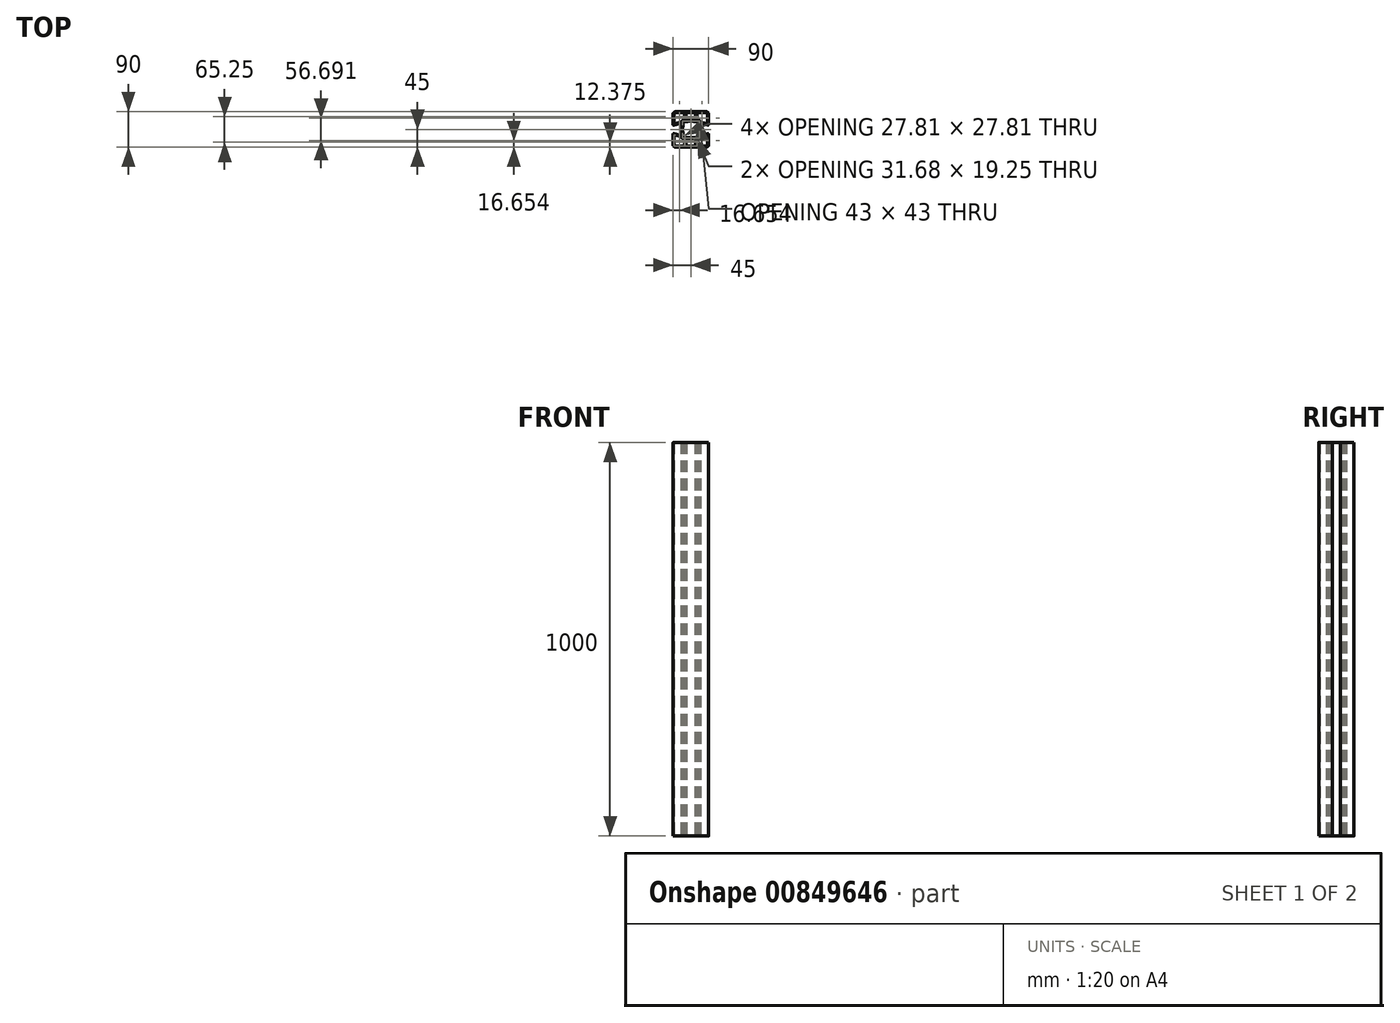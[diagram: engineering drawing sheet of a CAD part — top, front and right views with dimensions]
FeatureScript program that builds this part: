
annotation { "Feature Type Name" : "Feature", "Feature Type Description" : "" }
export const myFeature = defineFeature(function(context is Context, id is Id, definition is map)
    precondition{}
    {
        {
            var Q0;
            Q0=qCreatedBy(makeId("Top.planeOp"),FACE);
            var sketch = newSketch(context, id + "F0", { "sketchPlane" : qUnion([Q0])});
            skLineSegment(sketch, "E0", {"start": v(-9.27, -23) * mm, "end": v(-14.84, -23) * mm});
            skLineSegment(sketch, "E1", {"start": v(-15.8, -24.26) * mm, "end": v(-10.99, -42.25) * mm});
            skLineSegment(sketch, "E2", {"start": v(-10.99, -42.25) * mm, "end": v(10.99, -42.25) * mm});
            skLineSegment(sketch, "E3", {"start": v(10.99, -42.25) * mm, "end": v(15.8, -24.26) * mm});
            skLineSegment(sketch, "E4", {"start": v(14.84, -23) * mm, "end": v(9.27, -23) * mm});
            skLineSegment(sketch, "E5", {"start": v(24.48, 18.6) * mm, "end": v(39.73, 14.5) * mm});
            skLineSegment(sketch, "E6", {"start": v(42.25, 16.44) * mm, "end": v(42.25, 39) * mm});
            skLineSegment(sketch, "E7", {"start": v(39, 42.25) * mm, "end": v(16.44, 42.25) * mm});
            skLineSegment(sketch, "E8", {"start": v(14.5, 39.73) * mm, "end": v(18.6, 24.48) * mm});
            skLineSegment(sketch, "E9", {"start": v(20.53, 23) * mm, "end": v(21, 23) * mm});
            skLineSegment(sketch, "E10", {"start": v(23, 21) * mm, "end": v(23, 20.53) * mm});
            skLineSegment(sketch, "E11", {"start": v(-18.6, 24.48) * mm, "end": v(-14.5, 39.73) * mm});
            skLineSegment(sketch, "E12", {"start": v(-16.44, 42.25) * mm, "end": v(-39, 42.25) * mm});
            skLineSegment(sketch, "E13", {"start": v(-42.25, 39) * mm, "end": v(-42.25, 16.44) * mm});
            skLineSegment(sketch, "E14", {"start": v(-39.73, 14.5) * mm, "end": v(-24.48, 18.6) * mm});
            skLineSegment(sketch, "E15", {"start": v(-23, 20.53) * mm, "end": v(-23, 21) * mm});
            skLineSegment(sketch, "E16", {"start": v(-21, 23) * mm, "end": v(-20.53, 23) * mm});
            skLineSegment(sketch, "E17", {"start": v(-19.25, -20.25) * mm, "end": v(-7.4, -20.25) * mm});
            skLineSegment(sketch, "E18", {"start": v(7.4, -20.25) * mm, "end": v(19.25, -20.25) * mm});
            skLineSegment(sketch, "E19", {"start": v(20.25, -19.25) * mm, "end": v(20.25, -7.4) * mm});
            skLineSegment(sketch, "E20", {"start": v(20.25, 7.4) * mm, "end": v(20.25, 19.25) * mm});
            skLineSegment(sketch, "E21", {"start": v(19.25, 20.25) * mm, "end": v(7.4, 20.25) * mm});
            skLineSegment(sketch, "E22", {"start": v(-7.4, 20.25) * mm, "end": v(-19.25, 20.25) * mm});
            skLineSegment(sketch, "E23", {"start": v(-20.25, 19.25) * mm, "end": v(-20.25, 7.4) * mm});
            skLineSegment(sketch, "E24", {"start": v(-20.25, -7.4) * mm, "end": v(-20.25, -19.25) * mm});
            skLineSegment(sketch, "E25", {"start": v(23, 9.27) * mm, "end": v(23, 14.84) * mm});
            skLineSegment(sketch, "E26", {"start": v(23, -14.84) * mm, "end": v(23, -9.27) * mm});
            skLineSegment(sketch, "E27", {"start": v(43.43, -10.67) * mm, "end": v(24.26, -15.8) * mm});
            skLineSegment(sketch, "E28", {"start": v(45, -39) * mm, "end": v(45, -11.88) * mm});
            skLineSegment(sketch, "E29", {"start": v(-39, -45) * mm, "end": v(39, -45) * mm});
            skLineSegment(sketch, "E30", {"start": v(-45, -11.88) * mm, "end": v(-45, -39) * mm});
            skLineSegment(sketch, "E31", {"start": v(-24.26, -15.8) * mm, "end": v(-43.43, -10.67) * mm});
            skLineSegment(sketch, "E32", {"start": v(-23, -9.27) * mm, "end": v(-23, -14.84) * mm});
            skLineSegment(sketch, "E33", {"start": v(-23, 14.84) * mm, "end": v(-23, 9.27) * mm});
            skLineSegment(sketch, "E34", {"start": v(-43.43, 10.67) * mm, "end": v(-24.26, 15.8) * mm});
            skLineSegment(sketch, "E35", {"start": v(-45, 39) * mm, "end": v(-45, 11.88) * mm});
            skLineSegment(sketch, "E36", {"start": v(39, 45) * mm, "end": v(-39, 45) * mm});
            skLineSegment(sketch, "E37", {"start": v(45, 11.88) * mm, "end": v(45, 39) * mm});
            skLineSegment(sketch, "E38", {"start": v(24.26, 15.8) * mm, "end": v(43.43, 10.67) * mm});
            skLineSegment(sketch, "E39", {"start": v(-10.99, 42.25) * mm, "end": v(-15.8, 24.26) * mm});
            skLineSegment(sketch, "E40", {"start": v(-14.84, 23) * mm, "end": v(-9.27, 23) * mm});
            skLineSegment(sketch, "E41", {"start": v(9.27, 23) * mm, "end": v(14.84, 23) * mm});
            skLineSegment(sketch, "E42", {"start": v(15.8, 24.26) * mm, "end": v(10.99, 42.25) * mm});
            skLineSegment(sketch, "E43", {"start": v(10.99, 42.25) * mm, "end": v(-10.99, 42.25) * mm});
            skLineSegment(sketch, "E44", {"start": v(-24.48, -18.6) * mm, "end": v(-39.73, -14.5) * mm});
            skLineSegment(sketch, "E45", {"start": v(-42.25, -16.44) * mm, "end": v(-42.25, -39) * mm});
            skLineSegment(sketch, "E46", {"start": v(-39, -42.25) * mm, "end": v(-16.44, -42.25) * mm});
            skLineSegment(sketch, "E47", {"start": v(-14.5, -39.73) * mm, "end": v(-18.6, -24.48) * mm});
            skLineSegment(sketch, "E48", {"start": v(-20.53, -23) * mm, "end": v(-21, -23) * mm});
            skLineSegment(sketch, "E49", {"start": v(-23, -21) * mm, "end": v(-23, -20.53) * mm});
            skLineSegment(sketch, "E50", {"start": v(18.6, -24.48) * mm, "end": v(14.5, -39.73) * mm});
            skLineSegment(sketch, "E51", {"start": v(16.44, -42.25) * mm, "end": v(39, -42.25) * mm});
            skLineSegment(sketch, "E52", {"start": v(42.25, -39) * mm, "end": v(42.25, -16.44) * mm});
            skLineSegment(sketch, "E53", {"start": v(39.73, -14.5) * mm, "end": v(24.48, -18.6) * mm});
            skLineSegment(sketch, "E54", {"start": v(23, -20.53) * mm, "end": v(23, -21) * mm});
            skLineSegment(sketch, "E55", {"start": v(21, -23) * mm, "end": v(20.53, -23) * mm});
            skArc(sketch, "E56", {"start": v(-8.86, -23.09) * mm, "mid": v(-9.06, -23.02) * mm, "end": v(-9.27, -23) * mm});
            skArc(sketch, "E57", {"start": v(-14.84, -23) * mm, "mid": v(-15.64, -23.4) * mm, "end": v(-15.8, -24.26) * mm});
            skArc(sketch, "E58", {"start": v(15.8, -24.26) * mm, "mid": v(15.64, -23.4) * mm, "end": v(14.84, -23) * mm});
            skArc(sketch, "E59", {"start": v(9.27, -23) * mm, "mid": v(9.06, -23.02) * mm, "end": v(8.86, -23.09) * mm});
            skArc(sketch, "E60", {"start": v(-8.86, -23.09) * mm, "mid": v(0, -25) * mm, "end": v(8.86, -23.09) * mm});
            skArc(sketch, "E61", {"start": v(23, 20.53) * mm, "mid": v(23.41, 19.3) * mm, "end": v(24.48, 18.6) * mm});
            skArc(sketch, "E62", {"start": v(39.73, 14.5) * mm, "mid": v(41.47, 14.85) * mm, "end": v(42.25, 16.44) * mm});
            skArc(sketch, "E63", {"start": v(42.25, 39) * mm, "mid": v(41.3, 41.3) * mm, "end": v(39, 42.25) * mm});
            skArc(sketch, "E64", {"start": v(16.44, 42.25) * mm, "mid": v(14.85, 41.47) * mm, "end": v(14.5, 39.73) * mm});
            skArc(sketch, "E65", {"start": v(18.6, 24.48) * mm, "mid": v(19.3, 23.41) * mm, "end": v(20.53, 23) * mm});
            skArc(sketch, "E66", {"start": v(23, 21) * mm, "mid": v(22.41, 22.41) * mm, "end": v(21, 23) * mm});
            skArc(sketch, "E67", {"start": v(-20.53, 23) * mm, "mid": v(-19.3, 23.41) * mm, "end": v(-18.6, 24.48) * mm});
            skArc(sketch, "E68", {"start": v(-14.5, 39.73) * mm, "mid": v(-14.85, 41.47) * mm, "end": v(-16.44, 42.25) * mm});
            skArc(sketch, "E69", {"start": v(-39, 42.25) * mm, "mid": v(-41.3, 41.3) * mm, "end": v(-42.25, 39) * mm});
            skArc(sketch, "E70", {"start": v(-42.25, 16.44) * mm, "mid": v(-41.47, 14.85) * mm, "end": v(-39.73, 14.5) * mm});
            skArc(sketch, "E71", {"start": v(-24.48, 18.6) * mm, "mid": v(-23.41, 19.3) * mm, "end": v(-23, 20.53) * mm});
            skArc(sketch, "E72", {"start": v(-21, 23) * mm, "mid": v(-22.41, 22.41) * mm, "end": v(-23, 21) * mm});
            skArc(sketch, "E73", {"start": v(-20.25, -19.25) * mm, "mid": v(-19.96, -19.96) * mm, "end": v(-19.25, -20.25) * mm});
            skArc(sketch, "E74", {"start": v(-7.07, -20.3) * mm, "mid": v(-7.23, -20.26) * mm, "end": v(-7.4, -20.25) * mm});
            skArc(sketch, "E75", {"start": v(-7.07, -20.3) * mm, "mid": v(0, -21.5) * mm, "end": v(7.07, -20.3) * mm});
            skArc(sketch, "E76", {"start": v(7.4, -20.25) * mm, "mid": v(7.23, -20.26) * mm, "end": v(7.07, -20.3) * mm});
            skArc(sketch, "E77", {"start": v(19.25, -20.25) * mm, "mid": v(19.96, -19.96) * mm, "end": v(20.25, -19.25) * mm});
            skArc(sketch, "E78", {"start": v(20.3, -7.07) * mm, "mid": v(20.26, -7.23) * mm, "end": v(20.25, -7.4) * mm});
            skArc(sketch, "E79", {"start": v(20.3, -7.07) * mm, "mid": v(21.5, 0) * mm, "end": v(20.3, 7.07) * mm});
            skArc(sketch, "E80", {"start": v(20.25, 7.4) * mm, "mid": v(20.26, 7.23) * mm, "end": v(20.3, 7.07) * mm});
            skArc(sketch, "E81", {"start": v(20.25, 19.25) * mm, "mid": v(19.96, 19.96) * mm, "end": v(19.25, 20.25) * mm});
            skArc(sketch, "E82", {"start": v(7.07, 20.3) * mm, "mid": v(7.23, 20.26) * mm, "end": v(7.4, 20.25) * mm});
            skArc(sketch, "E83", {"start": v(7.07, 20.3) * mm, "mid": v(0, 21.5) * mm, "end": v(-7.07, 20.3) * mm});
            skArc(sketch, "E84", {"start": v(-7.4, 20.25) * mm, "mid": v(-7.23, 20.26) * mm, "end": v(-7.07, 20.3) * mm});
            skArc(sketch, "E85", {"start": v(-19.25, 20.25) * mm, "mid": v(-19.96, 19.96) * mm, "end": v(-20.25, 19.25) * mm});
            skArc(sketch, "E86", {"start": v(-20.3, 7.07) * mm, "mid": v(-20.26, 7.23) * mm, "end": v(-20.25, 7.4) * mm});
            skArc(sketch, "E87", {"start": v(-20.3, 7.07) * mm, "mid": v(-21.5, 0) * mm, "end": v(-20.3, -7.07) * mm});
            skArc(sketch, "E88", {"start": v(-20.25, -7.4) * mm, "mid": v(-20.26, -7.23) * mm, "end": v(-20.3, -7.07) * mm});
            skArc(sketch, "E89", {"start": v(24.26, 15.8) * mm, "mid": v(23.4, 15.64) * mm, "end": v(23, 14.84) * mm});
            skArc(sketch, "E90", {"start": v(23, 9.27) * mm, "mid": v(23.02, 9.06) * mm, "end": v(23.09, 8.86) * mm});
            skArc(sketch, "E91", {"start": v(23.09, -8.86) * mm, "mid": v(25, 0) * mm, "end": v(23.09, 8.86) * mm});
            skArc(sketch, "E92", {"start": v(23.09, -8.86) * mm, "mid": v(23.02, -9.06) * mm, "end": v(23, -9.27) * mm});
            skArc(sketch, "E93", {"start": v(23, -14.84) * mm, "mid": v(23.4, -15.64) * mm, "end": v(24.26, -15.8) * mm});
            skArc(sketch, "E94", {"start": v(45, -11.88) * mm, "mid": v(44.51, -10.89) * mm, "end": v(43.43, -10.67) * mm});
            skArc(sketch, "E95", {"start": v(39, -45) * mm, "mid": v(43.24, -43.24) * mm, "end": v(45, -39) * mm});
            skArc(sketch, "E96", {"start": v(-45, -39) * mm, "mid": v(-43.24, -43.24) * mm, "end": v(-39, -45) * mm});
            skArc(sketch, "E97", {"start": v(-43.43, -10.67) * mm, "mid": v(-44.51, -10.89) * mm, "end": v(-45, -11.88) * mm});
            skArc(sketch, "E98", {"start": v(-24.26, -15.8) * mm, "mid": v(-23.4, -15.64) * mm, "end": v(-23, -14.84) * mm});
            skArc(sketch, "E99", {"start": v(-23, -9.27) * mm, "mid": v(-23.02, -9.06) * mm, "end": v(-23.09, -8.86) * mm});
            skArc(sketch, "E100", {"start": v(-23.09, 8.86) * mm, "mid": v(-25, 0) * mm, "end": v(-23.09, -8.86) * mm});
            skArc(sketch, "E101", {"start": v(-23.09, 8.86) * mm, "mid": v(-23.02, 9.06) * mm, "end": v(-23, 9.27) * mm});
            skArc(sketch, "E102", {"start": v(-23, 14.84) * mm, "mid": v(-23.4, 15.64) * mm, "end": v(-24.26, 15.8) * mm});
            skArc(sketch, "E103", {"start": v(-45, 11.88) * mm, "mid": v(-44.51, 10.89) * mm, "end": v(-43.43, 10.67) * mm});
            skArc(sketch, "E104", {"start": v(-39, 45) * mm, "mid": v(-43.24, 43.24) * mm, "end": v(-45, 39) * mm});
            skArc(sketch, "E105", {"start": v(45, 39) * mm, "mid": v(43.24, 43.24) * mm, "end": v(39, 45) * mm});
            skArc(sketch, "E106", {"start": v(43.43, 10.67) * mm, "mid": v(44.51, 10.89) * mm, "end": v(45, 11.88) * mm});
            skArc(sketch, "E107", {"start": v(-15.8, 24.26) * mm, "mid": v(-15.64, 23.4) * mm, "end": v(-14.84, 23) * mm});
            skArc(sketch, "E108", {"start": v(-9.27, 23) * mm, "mid": v(-9.06, 23.02) * mm, "end": v(-8.86, 23.09) * mm});
            skArc(sketch, "E109", {"start": v(8.86, 23.09) * mm, "mid": v(0, 25) * mm, "end": v(-8.86, 23.09) * mm});
            skArc(sketch, "E110", {"start": v(8.86, 23.09) * mm, "mid": v(9.06, 23.02) * mm, "end": v(9.27, 23) * mm});
            skArc(sketch, "E111", {"start": v(14.84, 23) * mm, "mid": v(15.64, 23.4) * mm, "end": v(15.8, 24.26) * mm});
            skArc(sketch, "E112", {"start": v(-23, -20.53) * mm, "mid": v(-23.41, -19.3) * mm, "end": v(-24.48, -18.6) * mm});
            skArc(sketch, "E113", {"start": v(-39.73, -14.5) * mm, "mid": v(-41.47, -14.85) * mm, "end": v(-42.25, -16.44) * mm});
            skArc(sketch, "E114", {"start": v(-42.25, -39) * mm, "mid": v(-41.3, -41.3) * mm, "end": v(-39, -42.25) * mm});
            skArc(sketch, "E115", {"start": v(-16.44, -42.25) * mm, "mid": v(-14.85, -41.47) * mm, "end": v(-14.5, -39.73) * mm});
            skArc(sketch, "E116", {"start": v(-18.6, -24.48) * mm, "mid": v(-19.3, -23.41) * mm, "end": v(-20.53, -23) * mm});
            skArc(sketch, "E117", {"start": v(-23, -21) * mm, "mid": v(-22.41, -22.41) * mm, "end": v(-21, -23) * mm});
            skArc(sketch, "E118", {"start": v(20.53, -23) * mm, "mid": v(19.3, -23.41) * mm, "end": v(18.6, -24.48) * mm});
            skArc(sketch, "E119", {"start": v(14.5, -39.73) * mm, "mid": v(14.85, -41.47) * mm, "end": v(16.44, -42.25) * mm});
            skArc(sketch, "E120", {"start": v(39, -42.25) * mm, "mid": v(41.3, -41.3) * mm, "end": v(42.25, -39) * mm});
            skArc(sketch, "E121", {"start": v(42.25, -16.44) * mm, "mid": v(41.47, -14.85) * mm, "end": v(39.73, -14.5) * mm});
            skArc(sketch, "E122", {"start": v(24.48, -18.6) * mm, "mid": v(23.41, -19.3) * mm, "end": v(23, -20.53) * mm});
            skArc(sketch, "E123", {"start": v(21, -23) * mm, "mid": v(22.41, -22.41) * mm, "end": v(23, -21) * mm});
            skArc(sketch, "E124.1.0.0", {"start": v(145, 39) * mm, "mid": v(143.24, 43.24) * mm, "end": v(139, 45) * mm});
            skLineSegment(sketch, "E124.1.0.1", {"start": v(55, -11.88) * mm, "end": v(55, -39) * mm});
            skLineSegment(sketch, "E124.1.0.2", {"start": v(145, 11.88) * mm, "end": v(145, 39) * mm});
            skArc(sketch, "E124.1.0.3", {"start": v(55, -39) * mm, "mid": v(56.76, -43.24) * mm, "end": v(61, -45) * mm});
            skLineSegment(sketch, "E124.1.0.4", {"start": v(57.75, -16.44) * mm, "end": v(57.75, -39) * mm});
            skLineSegment(sketch, "E124.1.0.5", {"start": v(61, -45) * mm, "end": v(139, -45) * mm});
            skArc(sketch, "E124.1.0.6", {"start": v(57.75, -39) * mm, "mid": v(58.7, -41.3) * mm, "end": v(61, -42.25) * mm});
            skLineSegment(sketch, "E124.1.0.7", {"start": v(55, 39) * mm, "end": v(55, 11.88) * mm});
            skArc(sketch, "E124.1.0.8", {"start": v(61, 42.25) * mm, "mid": v(58.7, 41.3) * mm, "end": v(57.75, 39) * mm});
            skArc(sketch, "E124.1.0.9", {"start": v(61, 45) * mm, "mid": v(56.76, 43.24) * mm, "end": v(55, 39) * mm});
            skLineSegment(sketch, "E124.1.0.10", {"start": v(57.75, 39) * mm, "end": v(57.75, 16.44) * mm});
            skArc(sketch, "E124.1.0.11", {"start": v(142.25, 39) * mm, "mid": v(141.3, 41.3) * mm, "end": v(139, 42.25) * mm});
            skLineSegment(sketch, "E124.1.0.12", {"start": v(139, 45) * mm, "end": v(61, 45) * mm});
            skLineSegment(sketch, "E124.1.0.13", {"start": v(142.25, 16.44) * mm, "end": v(142.25, 39) * mm});
            skLineSegment(sketch, "E124.1.0.14", {"start": v(110.99, 42.25) * mm, "end": v(89.01, 42.25) * mm});
            skArc(sketch, "E124.1.0.15", {"start": v(85.5, 39.73) * mm, "mid": v(85.15, 41.47) * mm, "end": v(83.56, 42.25) * mm});
            skLineSegment(sketch, "E124.1.0.16", {"start": v(139, 42.25) * mm, "end": v(116.44, 42.25) * mm});
            skLineSegment(sketch, "E124.1.0.17", {"start": v(124.26, 15.8) * mm, "end": v(143.43, 10.67) * mm});
            skArc(sketch, "E124.1.0.18", {"start": v(139.73, 14.5) * mm, "mid": v(141.47, 14.85) * mm, "end": v(142.25, 16.44) * mm});
            skLineSegment(sketch, "E124.1.0.19", {"start": v(83.56, 42.25) * mm, "end": v(61, 42.25) * mm});
            skArc(sketch, "E124.1.0.20", {"start": v(91.14, -23.09) * mm, "mid": v(100, -25) * mm, "end": v(108.86, -23.09) * mm});
            skLineSegment(sketch, "E124.1.0.21", {"start": v(60.27, 14.5) * mm, "end": v(75.52, 18.6) * mm});
            skArc(sketch, "E124.1.0.22", {"start": v(57.75, 16.44) * mm, "mid": v(58.53, 14.85) * mm, "end": v(60.27, 14.5) * mm});
            skArc(sketch, "E124.1.0.23", {"start": v(108.86, 23.09) * mm, "mid": v(109.06, 23.02) * mm, "end": v(109.27, 23) * mm});
            skArc(sketch, "E124.1.0.24", {"start": v(120.25, 7.4) * mm, "mid": v(120.26, 7.23) * mm, "end": v(120.3, 7.07) * mm});
            skArc(sketch, "E124.1.0.25", {"start": v(114.5, -39.73) * mm, "mid": v(114.85, -41.47) * mm, "end": v(116.44, -42.25) * mm});
            skArc(sketch, "E124.1.0.26", {"start": v(120.53, -23) * mm, "mid": v(119.3, -23.41) * mm, "end": v(118.6, -24.48) * mm});
            skArc(sketch, "E124.1.0.27", {"start": v(79.75, -7.4) * mm, "mid": v(79.74, -7.23) * mm, "end": v(79.7, -7.07) * mm});
            skArc(sketch, "E124.1.0.28", {"start": v(139, -42.25) * mm, "mid": v(141.3, -41.3) * mm, "end": v(142.25, -39) * mm});
            skLineSegment(sketch, "E124.1.0.29", {"start": v(116.44, -42.25) * mm, "end": v(139, -42.25) * mm});
            skArc(sketch, "E124.1.0.30", {"start": v(145, -11.88) * mm, "mid": v(144.51, -10.89) * mm, "end": v(143.43, -10.67) * mm});
            skArc(sketch, "E124.1.0.31", {"start": v(83.56, -42.25) * mm, "mid": v(85.15, -41.47) * mm, "end": v(85.5, -39.73) * mm});
            skArc(sketch, "E124.1.0.32", {"start": v(55, 11.88) * mm, "mid": v(55.49, 10.89) * mm, "end": v(56.57, 10.67) * mm});
            skLineSegment(sketch, "E124.1.0.33", {"start": v(80.75, -20.25) * mm, "end": v(92.6, -20.25) * mm});
            skArc(sketch, "E124.1.0.34", {"start": v(108.86, 23.09) * mm, "mid": v(100, 25) * mm, "end": v(91.14, 23.09) * mm});
            skArc(sketch, "E124.1.0.35", {"start": v(139, -45) * mm, "mid": v(143.24, -43.24) * mm, "end": v(145, -39) * mm});
            skLineSegment(sketch, "E124.1.0.36", {"start": v(139.73, -14.5) * mm, "end": v(124.48, -18.6) * mm});
            skLineSegment(sketch, "E124.1.0.37", {"start": v(124.48, 18.6) * mm, "end": v(139.73, 14.5) * mm});
            skArc(sketch, "E124.1.0.38", {"start": v(120.3, -7.07) * mm, "mid": v(120.26, -7.23) * mm, "end": v(120.25, -7.4) * mm});
            skArc(sketch, "E124.1.0.39", {"start": v(116.44, 42.25) * mm, "mid": v(114.85, 41.47) * mm, "end": v(114.5, 39.73) * mm});
            skArc(sketch, "E124.1.0.40", {"start": v(123.09, -8.86) * mm, "mid": v(125, 0) * mm, "end": v(123.09, 8.86) * mm});
            skArc(sketch, "E124.1.0.41", {"start": v(118.6, 24.48) * mm, "mid": v(119.3, 23.41) * mm, "end": v(120.53, 23) * mm});
            skArc(sketch, "E124.1.0.42", {"start": v(56.57, -10.67) * mm, "mid": v(55.49, -10.89) * mm, "end": v(55, -11.88) * mm});
            skLineSegment(sketch, "E124.1.0.43", {"start": v(77, -21) * mm, "end": v(77, -20.53) * mm});
            skLineSegment(sketch, "E124.1.0.44", {"start": v(61, -42.25) * mm, "end": v(83.56, -42.25) * mm});
            skLineSegment(sketch, "E124.1.0.45", {"start": v(85.16, 23) * mm, "end": v(90.73, 23) * mm});
            skLineSegment(sketch, "E124.1.0.46", {"start": v(92.6, 20.25) * mm, "end": v(80.75, 20.25) * mm});
            skLineSegment(sketch, "E124.1.0.47", {"start": v(145, -39) * mm, "end": v(145, -11.88) * mm});
            skLineSegment(sketch, "E124.1.0.48", {"start": v(89.01, -42.25) * mm, "end": v(110.99, -42.25) * mm});
            skLineSegment(sketch, "E124.1.0.49", {"start": v(89.01, 42.25) * mm, "end": v(84.2, 24.26) * mm});
            skLineSegment(sketch, "E124.1.0.50", {"start": v(77, 14.84) * mm, "end": v(77, 9.27) * mm});
            skArc(sketch, "E124.1.0.51", {"start": v(120.25, 19.25) * mm, "mid": v(119.96, 19.96) * mm, "end": v(119.25, 20.25) * mm});
            skArc(sketch, "E124.1.0.52", {"start": v(92.93, -20.3) * mm, "mid": v(100, -21.5) * mm, "end": v(107.07, -20.3) * mm});
            skArc(sketch, "E124.1.0.53", {"start": v(107.07, 20.3) * mm, "mid": v(100, 21.5) * mm, "end": v(92.93, 20.3) * mm});
            skArc(sketch, "E124.1.0.54", {"start": v(77, -21) * mm, "mid": v(77.59, -22.41) * mm, "end": v(79, -23) * mm});
            skLineSegment(sketch, "E124.1.0.55", {"start": v(81.4, 24.48) * mm, "end": v(85.5, 39.73) * mm});
            skArc(sketch, "E124.1.0.56", {"start": v(107.4, -20.25) * mm, "mid": v(107.23, -20.26) * mm, "end": v(107.07, -20.3) * mm});
            skLineSegment(sketch, "E124.1.0.57", {"start": v(119.25, 20.25) * mm, "end": v(107.4, 20.25) * mm});
            skArc(sketch, "E124.1.0.58", {"start": v(76.91, 8.86) * mm, "mid": v(76.98, 9.06) * mm, "end": v(77, 9.27) * mm});
            skArc(sketch, "E124.1.0.59", {"start": v(119.25, -20.25) * mm, "mid": v(119.96, -19.96) * mm, "end": v(120.25, -19.25) * mm});
            skArc(sketch, "E124.1.0.60", {"start": v(123.09, -8.86) * mm, "mid": v(123.02, -9.06) * mm, "end": v(123, -9.27) * mm});
            skLineSegment(sketch, "E124.1.0.61", {"start": v(114.5, 39.73) * mm, "end": v(118.6, 24.48) * mm});
            skArc(sketch, "E124.1.0.62", {"start": v(80.75, 20.25) * mm, "mid": v(80.04, 19.96) * mm, "end": v(79.75, 19.25) * mm});
            skLineSegment(sketch, "E124.1.0.63", {"start": v(56.57, 10.67) * mm, "end": v(75.74, 15.8) * mm});
            skLineSegment(sketch, "E124.1.0.64", {"start": v(120.25, 7.4) * mm, "end": v(120.25, 19.25) * mm});
            skLineSegment(sketch, "E124.1.0.65", {"start": v(142.25, -39) * mm, "end": v(142.25, -16.44) * mm});
            skArc(sketch, "E124.1.0.66", {"start": v(91.14, -23.09) * mm, "mid": v(90.94, -23.02) * mm, "end": v(90.73, -23) * mm});
            skArc(sketch, "E124.1.0.67", {"start": v(120.3, -7.07) * mm, "mid": v(121.5, 0) * mm, "end": v(120.3, 7.07) * mm});
            skArc(sketch, "E124.1.0.68", {"start": v(60.27, -14.5) * mm, "mid": v(58.53, -14.85) * mm, "end": v(57.75, -16.44) * mm});
            skArc(sketch, "E124.1.0.69", {"start": v(143.43, 10.67) * mm, "mid": v(144.51, 10.89) * mm, "end": v(145, 11.88) * mm});
            skArc(sketch, "E124.1.0.70", {"start": v(90.73, 23) * mm, "mid": v(90.94, 23.02) * mm, "end": v(91.14, 23.09) * mm});
            skLineSegment(sketch, "E124.1.0.71", {"start": v(143.43, -10.67) * mm, "end": v(124.26, -15.8) * mm});
            skLineSegment(sketch, "E124.1.0.72", {"start": v(114.84, -23) * mm, "end": v(109.27, -23) * mm});
            skLineSegment(sketch, "E124.1.0.73", {"start": v(85.5, -39.73) * mm, "end": v(81.4, -24.48) * mm});
            skLineSegment(sketch, "E124.1.0.74", {"start": v(110.99, -42.25) * mm, "end": v(115.8, -24.26) * mm});
            skLineSegment(sketch, "E124.1.0.75", {"start": v(79.75, -7.4) * mm, "end": v(79.75, -19.25) * mm});
            skLineSegment(sketch, "E124.1.0.76", {"start": v(77, -9.27) * mm, "end": v(77, -14.84) * mm});
            skLineSegment(sketch, "E124.1.0.77", {"start": v(121, -23) * mm, "end": v(120.53, -23) * mm});
            skArc(sketch, "E124.1.0.78", {"start": v(115.8, -24.26) * mm, "mid": v(115.64, -23.4) * mm, "end": v(114.84, -23) * mm});
            skArc(sketch, "E124.1.0.79", {"start": v(114.84, 23) * mm, "mid": v(115.64, 23.4) * mm, "end": v(115.8, 24.26) * mm});
            skArc(sketch, "E124.1.0.80", {"start": v(79, 23) * mm, "mid": v(77.59, 22.41) * mm, "end": v(77, 21) * mm});
            skLineSegment(sketch, "E124.1.0.81", {"start": v(118.6, -24.48) * mm, "end": v(114.5, -39.73) * mm});
            skArc(sketch, "E124.1.0.82", {"start": v(76.91, 8.86) * mm, "mid": v(75, 0) * mm, "end": v(76.91, -8.86) * mm});
            skArc(sketch, "E124.1.0.83", {"start": v(123, -14.84) * mm, "mid": v(123.4, -15.64) * mm, "end": v(124.26, -15.8) * mm});
            skArc(sketch, "E124.1.0.84", {"start": v(92.6, 20.25) * mm, "mid": v(92.77, 20.26) * mm, "end": v(92.93, 20.3) * mm});
            skLineSegment(sketch, "E124.1.0.85", {"start": v(79.47, -23) * mm, "end": v(79, -23) * mm});
            skLineSegment(sketch, "E124.1.0.86", {"start": v(115.8, 24.26) * mm, "end": v(110.99, 42.25) * mm});
            skArc(sketch, "E124.1.0.87", {"start": v(123, 20.53) * mm, "mid": v(123.41, 19.3) * mm, "end": v(124.48, 18.6) * mm});
            skArc(sketch, "E124.1.0.88", {"start": v(109.27, -23) * mm, "mid": v(109.06, -23.02) * mm, "end": v(108.86, -23.09) * mm});
            skLineSegment(sketch, "E124.1.0.89", {"start": v(84.2, -24.26) * mm, "end": v(89.01, -42.25) * mm});
            skArc(sketch, "E124.1.0.90", {"start": v(92.93, -20.3) * mm, "mid": v(92.77, -20.26) * mm, "end": v(92.6, -20.25) * mm});
            skArc(sketch, "E124.1.0.91", {"start": v(142.25, -16.44) * mm, "mid": v(141.47, -14.85) * mm, "end": v(139.73, -14.5) * mm});
            skLineSegment(sketch, "E124.1.0.92", {"start": v(75.52, -18.6) * mm, "end": v(60.27, -14.5) * mm});
            skLineSegment(sketch, "E124.1.0.93", {"start": v(123, 9.27) * mm, "end": v(123, 14.84) * mm});
            skArc(sketch, "E124.1.0.94", {"start": v(107.07, 20.3) * mm, "mid": v(107.23, 20.26) * mm, "end": v(107.4, 20.25) * mm});
            skLineSegment(sketch, "E124.1.0.95", {"start": v(109.27, 23) * mm, "end": v(114.84, 23) * mm});
            skArc(sketch, "E124.1.0.96", {"start": v(121, -23) * mm, "mid": v(122.41, -22.41) * mm, "end": v(123, -21) * mm});
            skArc(sketch, "E124.1.0.97", {"start": v(77, -20.53) * mm, "mid": v(76.59, -19.3) * mm, "end": v(75.52, -18.6) * mm});
            skLineSegment(sketch, "E124.1.0.98", {"start": v(79, 23) * mm, "end": v(79.47, 23) * mm});
            skLineSegment(sketch, "E124.1.0.99", {"start": v(120.25, -19.25) * mm, "end": v(120.25, -7.4) * mm});
            skArc(sketch, "E124.1.0.100", {"start": v(84.2, 24.26) * mm, "mid": v(84.36, 23.4) * mm, "end": v(85.16, 23) * mm});
            skLineSegment(sketch, "E124.1.0.101", {"start": v(107.4, -20.25) * mm, "end": v(119.25, -20.25) * mm});
            skLineSegment(sketch, "E124.1.0.102", {"start": v(123, 21) * mm, "end": v(123, 20.53) * mm});
            skLineSegment(sketch, "E124.1.0.103", {"start": v(90.73, -23) * mm, "end": v(85.16, -23) * mm});
            skLineSegment(sketch, "E124.1.0.104", {"start": v(75.74, -15.8) * mm, "end": v(56.57, -10.67) * mm});
            skArc(sketch, "E124.1.0.105", {"start": v(79.7, 7.07) * mm, "mid": v(78.5, 0) * mm, "end": v(79.7, -7.07) * mm});
            skArc(sketch, "E124.1.0.106", {"start": v(123, 9.27) * mm, "mid": v(123.02, 9.06) * mm, "end": v(123.09, 8.86) * mm});
            skArc(sketch, "E124.1.0.107", {"start": v(81.4, -24.48) * mm, "mid": v(80.7, -23.41) * mm, "end": v(79.47, -23) * mm});
            skLineSegment(sketch, "E124.1.0.108", {"start": v(123, -20.53) * mm, "end": v(123, -21) * mm});
            skArc(sketch, "E124.1.0.109", {"start": v(79.47, 23) * mm, "mid": v(80.7, 23.41) * mm, "end": v(81.4, 24.48) * mm});
            skArc(sketch, "E124.1.0.110", {"start": v(77, -9.27) * mm, "mid": v(76.98, -9.06) * mm, "end": v(76.91, -8.86) * mm});
            skLineSegment(sketch, "E124.1.0.111", {"start": v(123, -14.84) * mm, "end": v(123, -9.27) * mm});
            skLineSegment(sketch, "E124.1.0.112", {"start": v(120.53, 23) * mm, "end": v(121, 23) * mm});
            skArc(sketch, "E124.1.0.113", {"start": v(75.52, 18.6) * mm, "mid": v(76.59, 19.3) * mm, "end": v(77, 20.53) * mm});
            skArc(sketch, "E124.1.0.114", {"start": v(85.16, -23) * mm, "mid": v(84.36, -23.4) * mm, "end": v(84.2, -24.26) * mm});
            skArc(sketch, "E124.1.0.115", {"start": v(75.74, -15.8) * mm, "mid": v(76.6, -15.64) * mm, "end": v(77, -14.84) * mm});
            skArc(sketch, "E124.1.0.116", {"start": v(124.48, -18.6) * mm, "mid": v(123.41, -19.3) * mm, "end": v(123, -20.53) * mm});
            skLineSegment(sketch, "E124.1.0.117", {"start": v(79.75, 19.25) * mm, "end": v(79.75, 7.4) * mm});
            skArc(sketch, "E124.1.0.118", {"start": v(79.75, -19.25) * mm, "mid": v(80.04, -19.96) * mm, "end": v(80.75, -20.25) * mm});
            skArc(sketch, "E124.1.0.119", {"start": v(123, 21) * mm, "mid": v(122.41, 22.41) * mm, "end": v(121, 23) * mm});
            skArc(sketch, "E124.1.0.120", {"start": v(124.26, 15.8) * mm, "mid": v(123.4, 15.64) * mm, "end": v(123, 14.84) * mm});
            skArc(sketch, "E124.1.0.121", {"start": v(77, 14.84) * mm, "mid": v(76.6, 15.64) * mm, "end": v(75.74, 15.8) * mm});
            skArc(sketch, "E124.1.0.122", {"start": v(79.7, 7.07) * mm, "mid": v(79.74, 7.23) * mm, "end": v(79.75, 7.4) * mm});
            skLineSegment(sketch, "E124.1.0.123", {"start": v(77, 20.53) * mm, "end": v(77, 21) * mm});
            skArc(sketch, "E124.2.0.0", {"start": v(245, 39) * mm, "mid": v(243.24, 43.24) * mm, "end": v(239, 45) * mm});
            skLineSegment(sketch, "E124.2.0.1", {"start": v(155, -11.88) * mm, "end": v(155, -39) * mm});
            skLineSegment(sketch, "E124.2.0.2", {"start": v(245, 11.88) * mm, "end": v(245, 39) * mm});
            skArc(sketch, "E124.2.0.3", {"start": v(155, -39) * mm, "mid": v(156.76, -43.24) * mm, "end": v(161, -45) * mm});
            skLineSegment(sketch, "E124.2.0.4", {"start": v(157.75, -16.44) * mm, "end": v(157.75, -39) * mm});
            skLineSegment(sketch, "E124.2.0.5", {"start": v(161, -45) * mm, "end": v(239, -45) * mm});
            skArc(sketch, "E124.2.0.6", {"start": v(157.75, -39) * mm, "mid": v(158.7, -41.3) * mm, "end": v(161, -42.25) * mm});
            skLineSegment(sketch, "E124.2.0.7", {"start": v(155, 39) * mm, "end": v(155, 11.88) * mm});
            skArc(sketch, "E124.2.0.8", {"start": v(161, 42.25) * mm, "mid": v(158.7, 41.3) * mm, "end": v(157.75, 39) * mm});
            skArc(sketch, "E124.2.0.9", {"start": v(161, 45) * mm, "mid": v(156.76, 43.24) * mm, "end": v(155, 39) * mm});
            skLineSegment(sketch, "E124.2.0.10", {"start": v(157.75, 39) * mm, "end": v(157.75, 16.44) * mm});
            skArc(sketch, "E124.2.0.11", {"start": v(242.25, 39) * mm, "mid": v(241.3, 41.3) * mm, "end": v(239, 42.25) * mm});
            skLineSegment(sketch, "E124.2.0.12", {"start": v(239, 45) * mm, "end": v(161, 45) * mm});
            skLineSegment(sketch, "E124.2.0.13", {"start": v(242.25, 16.44) * mm, "end": v(242.25, 39) * mm});
            skLineSegment(sketch, "E124.2.0.14", {"start": v(210.99, 42.25) * mm, "end": v(189.01, 42.25) * mm});
            skArc(sketch, "E124.2.0.15", {"start": v(185.5, 39.73) * mm, "mid": v(185.15, 41.47) * mm, "end": v(183.56, 42.25) * mm});
            skLineSegment(sketch, "E124.2.0.16", {"start": v(239, 42.25) * mm, "end": v(216.44, 42.25) * mm});
            skLineSegment(sketch, "E124.2.0.17", {"start": v(224.26, 15.8) * mm, "end": v(243.43, 10.67) * mm});
            skArc(sketch, "E124.2.0.18", {"start": v(239.73, 14.5) * mm, "mid": v(241.47, 14.85) * mm, "end": v(242.25, 16.44) * mm});
            skLineSegment(sketch, "E124.2.0.19", {"start": v(183.56, 42.25) * mm, "end": v(161, 42.25) * mm});
            skArc(sketch, "E124.2.0.20", {"start": v(191.14, -23.09) * mm, "mid": v(200, -25) * mm, "end": v(208.86, -23.09) * mm});
            skLineSegment(sketch, "E124.2.0.21", {"start": v(160.27, 14.5) * mm, "end": v(175.52, 18.6) * mm});
            skArc(sketch, "E124.2.0.22", {"start": v(157.75, 16.44) * mm, "mid": v(158.53, 14.85) * mm, "end": v(160.27, 14.5) * mm});
            skArc(sketch, "E124.2.0.23", {"start": v(208.86, 23.09) * mm, "mid": v(209.06, 23.02) * mm, "end": v(209.27, 23) * mm});
            skArc(sketch, "E124.2.0.24", {"start": v(220.25, 7.4) * mm, "mid": v(220.26, 7.23) * mm, "end": v(220.3, 7.07) * mm});
            skArc(sketch, "E124.2.0.25", {"start": v(214.5, -39.73) * mm, "mid": v(214.85, -41.47) * mm, "end": v(216.44, -42.25) * mm});
            skArc(sketch, "E124.2.0.26", {"start": v(220.53, -23) * mm, "mid": v(219.3, -23.41) * mm, "end": v(218.6, -24.48) * mm});
            skArc(sketch, "E124.2.0.27", {"start": v(179.75, -7.4) * mm, "mid": v(179.74, -7.23) * mm, "end": v(179.7, -7.07) * mm});
            skArc(sketch, "E124.2.0.28", {"start": v(239, -42.25) * mm, "mid": v(241.3, -41.3) * mm, "end": v(242.25, -39) * mm});
            skLineSegment(sketch, "E124.2.0.29", {"start": v(216.44, -42.25) * mm, "end": v(239, -42.25) * mm});
            skArc(sketch, "E124.2.0.30", {"start": v(245, -11.88) * mm, "mid": v(244.51, -10.89) * mm, "end": v(243.43, -10.67) * mm});
            skArc(sketch, "E124.2.0.31", {"start": v(183.56, -42.25) * mm, "mid": v(185.15, -41.47) * mm, "end": v(185.5, -39.73) * mm});
            skArc(sketch, "E124.2.0.32", {"start": v(155, 11.88) * mm, "mid": v(155.49, 10.89) * mm, "end": v(156.57, 10.67) * mm});
            skLineSegment(sketch, "E124.2.0.33", {"start": v(180.75, -20.25) * mm, "end": v(192.6, -20.25) * mm});
            skArc(sketch, "E124.2.0.34", {"start": v(208.86, 23.09) * mm, "mid": v(200, 25) * mm, "end": v(191.14, 23.09) * mm});
            skArc(sketch, "E124.2.0.35", {"start": v(239, -45) * mm, "mid": v(243.24, -43.24) * mm, "end": v(245, -39) * mm});
            skLineSegment(sketch, "E124.2.0.36", {"start": v(239.73, -14.5) * mm, "end": v(224.48, -18.6) * mm});
            skLineSegment(sketch, "E124.2.0.37", {"start": v(224.48, 18.6) * mm, "end": v(239.73, 14.5) * mm});
            skArc(sketch, "E124.2.0.38", {"start": v(220.3, -7.07) * mm, "mid": v(220.26, -7.23) * mm, "end": v(220.25, -7.4) * mm});
            skArc(sketch, "E124.2.0.39", {"start": v(216.44, 42.25) * mm, "mid": v(214.85, 41.47) * mm, "end": v(214.5, 39.73) * mm});
            skArc(sketch, "E124.2.0.40", {"start": v(223.09, -8.86) * mm, "mid": v(225, 0) * mm, "end": v(223.09, 8.86) * mm});
            skArc(sketch, "E124.2.0.41", {"start": v(218.6, 24.48) * mm, "mid": v(219.3, 23.41) * mm, "end": v(220.53, 23) * mm});
            skArc(sketch, "E124.2.0.42", {"start": v(156.57, -10.67) * mm, "mid": v(155.49, -10.89) * mm, "end": v(155, -11.88) * mm});
            skLineSegment(sketch, "E124.2.0.43", {"start": v(177, -21) * mm, "end": v(177, -20.53) * mm});
            skLineSegment(sketch, "E124.2.0.44", {"start": v(161, -42.25) * mm, "end": v(183.56, -42.25) * mm});
            skLineSegment(sketch, "E124.2.0.45", {"start": v(185.16, 23) * mm, "end": v(190.73, 23) * mm});
            skLineSegment(sketch, "E124.2.0.46", {"start": v(192.6, 20.25) * mm, "end": v(180.75, 20.25) * mm});
            skLineSegment(sketch, "E124.2.0.47", {"start": v(245, -39) * mm, "end": v(245, -11.88) * mm});
            skLineSegment(sketch, "E124.2.0.48", {"start": v(189.01, -42.25) * mm, "end": v(210.99, -42.25) * mm});
            skLineSegment(sketch, "E124.2.0.49", {"start": v(189.01, 42.25) * mm, "end": v(184.2, 24.26) * mm});
            skLineSegment(sketch, "E124.2.0.50", {"start": v(177, 14.84) * mm, "end": v(177, 9.27) * mm});
            skArc(sketch, "E124.2.0.51", {"start": v(220.25, 19.25) * mm, "mid": v(219.96, 19.96) * mm, "end": v(219.25, 20.25) * mm});
            skArc(sketch, "E124.2.0.52", {"start": v(192.93, -20.3) * mm, "mid": v(200, -21.5) * mm, "end": v(207.07, -20.3) * mm});
            skArc(sketch, "E124.2.0.53", {"start": v(207.07, 20.3) * mm, "mid": v(200, 21.5) * mm, "end": v(192.93, 20.3) * mm});
            skArc(sketch, "E124.2.0.54", {"start": v(177, -21) * mm, "mid": v(177.59, -22.41) * mm, "end": v(179, -23) * mm});
            skLineSegment(sketch, "E124.2.0.55", {"start": v(181.4, 24.48) * mm, "end": v(185.5, 39.73) * mm});
            skArc(sketch, "E124.2.0.56", {"start": v(207.4, -20.25) * mm, "mid": v(207.23, -20.26) * mm, "end": v(207.07, -20.3) * mm});
            skLineSegment(sketch, "E124.2.0.57", {"start": v(219.25, 20.25) * mm, "end": v(207.4, 20.25) * mm});
            skArc(sketch, "E124.2.0.58", {"start": v(176.91, 8.86) * mm, "mid": v(176.98, 9.06) * mm, "end": v(177, 9.27) * mm});
            skArc(sketch, "E124.2.0.59", {"start": v(219.25, -20.25) * mm, "mid": v(219.96, -19.96) * mm, "end": v(220.25, -19.25) * mm});
            skArc(sketch, "E124.2.0.60", {"start": v(223.09, -8.86) * mm, "mid": v(223.02, -9.06) * mm, "end": v(223, -9.27) * mm});
            skLineSegment(sketch, "E124.2.0.61", {"start": v(214.5, 39.73) * mm, "end": v(218.6, 24.48) * mm});
            skArc(sketch, "E124.2.0.62", {"start": v(180.75, 20.25) * mm, "mid": v(180.04, 19.96) * mm, "end": v(179.75, 19.25) * mm});
            skLineSegment(sketch, "E124.2.0.63", {"start": v(156.57, 10.67) * mm, "end": v(175.74, 15.8) * mm});
            skLineSegment(sketch, "E124.2.0.64", {"start": v(220.25, 7.4) * mm, "end": v(220.25, 19.25) * mm});
            skLineSegment(sketch, "E124.2.0.65", {"start": v(242.25, -39) * mm, "end": v(242.25, -16.44) * mm});
            skArc(sketch, "E124.2.0.66", {"start": v(191.14, -23.09) * mm, "mid": v(190.94, -23.02) * mm, "end": v(190.73, -23) * mm});
            skArc(sketch, "E124.2.0.67", {"start": v(220.3, -7.07) * mm, "mid": v(221.5, 0) * mm, "end": v(220.3, 7.07) * mm});
            skArc(sketch, "E124.2.0.68", {"start": v(160.27, -14.5) * mm, "mid": v(158.53, -14.85) * mm, "end": v(157.75, -16.44) * mm});
            skArc(sketch, "E124.2.0.69", {"start": v(243.43, 10.67) * mm, "mid": v(244.51, 10.89) * mm, "end": v(245, 11.88) * mm});
            skArc(sketch, "E124.2.0.70", {"start": v(190.73, 23) * mm, "mid": v(190.94, 23.02) * mm, "end": v(191.14, 23.09) * mm});
            skLineSegment(sketch, "E124.2.0.71", {"start": v(243.43, -10.67) * mm, "end": v(224.26, -15.8) * mm});
            skLineSegment(sketch, "E124.2.0.72", {"start": v(214.84, -23) * mm, "end": v(209.27, -23) * mm});
            skLineSegment(sketch, "E124.2.0.73", {"start": v(185.5, -39.73) * mm, "end": v(181.4, -24.48) * mm});
            skLineSegment(sketch, "E124.2.0.74", {"start": v(210.99, -42.25) * mm, "end": v(215.8, -24.26) * mm});
            skLineSegment(sketch, "E124.2.0.75", {"start": v(179.75, -7.4) * mm, "end": v(179.75, -19.25) * mm});
            skLineSegment(sketch, "E124.2.0.76", {"start": v(177, -9.27) * mm, "end": v(177, -14.84) * mm});
            skLineSegment(sketch, "E124.2.0.77", {"start": v(221, -23) * mm, "end": v(220.53, -23) * mm});
            skArc(sketch, "E124.2.0.78", {"start": v(215.8, -24.26) * mm, "mid": v(215.64, -23.4) * mm, "end": v(214.84, -23) * mm});
            skArc(sketch, "E124.2.0.79", {"start": v(214.84, 23) * mm, "mid": v(215.64, 23.4) * mm, "end": v(215.8, 24.26) * mm});
            skArc(sketch, "E124.2.0.80", {"start": v(179, 23) * mm, "mid": v(177.59, 22.41) * mm, "end": v(177, 21) * mm});
            skLineSegment(sketch, "E124.2.0.81", {"start": v(218.6, -24.48) * mm, "end": v(214.5, -39.73) * mm});
            skArc(sketch, "E124.2.0.82", {"start": v(176.91, 8.86) * mm, "mid": v(175, 0) * mm, "end": v(176.91, -8.86) * mm});
            skArc(sketch, "E124.2.0.83", {"start": v(223, -14.84) * mm, "mid": v(223.4, -15.64) * mm, "end": v(224.26, -15.8) * mm});
            skArc(sketch, "E124.2.0.84", {"start": v(192.6, 20.25) * mm, "mid": v(192.77, 20.26) * mm, "end": v(192.93, 20.3) * mm});
            skLineSegment(sketch, "E124.2.0.85", {"start": v(179.47, -23) * mm, "end": v(179, -23) * mm});
            skLineSegment(sketch, "E124.2.0.86", {"start": v(215.8, 24.26) * mm, "end": v(210.99, 42.25) * mm});
            skArc(sketch, "E124.2.0.87", {"start": v(223, 20.53) * mm, "mid": v(223.41, 19.3) * mm, "end": v(224.48, 18.6) * mm});
            skArc(sketch, "E124.2.0.88", {"start": v(209.27, -23) * mm, "mid": v(209.06, -23.02) * mm, "end": v(208.86, -23.09) * mm});
            skLineSegment(sketch, "E124.2.0.89", {"start": v(184.2, -24.26) * mm, "end": v(189.01, -42.25) * mm});
            skArc(sketch, "E124.2.0.90", {"start": v(192.93, -20.3) * mm, "mid": v(192.77, -20.26) * mm, "end": v(192.6, -20.25) * mm});
            skArc(sketch, "E124.2.0.91", {"start": v(242.25, -16.44) * mm, "mid": v(241.47, -14.85) * mm, "end": v(239.73, -14.5) * mm});
            skLineSegment(sketch, "E124.2.0.92", {"start": v(175.52, -18.6) * mm, "end": v(160.27, -14.5) * mm});
            skLineSegment(sketch, "E124.2.0.93", {"start": v(223, 9.27) * mm, "end": v(223, 14.84) * mm});
            skArc(sketch, "E124.2.0.94", {"start": v(207.07, 20.3) * mm, "mid": v(207.23, 20.26) * mm, "end": v(207.4, 20.25) * mm});
            skLineSegment(sketch, "E124.2.0.95", {"start": v(209.27, 23) * mm, "end": v(214.84, 23) * mm});
            skArc(sketch, "E124.2.0.96", {"start": v(221, -23) * mm, "mid": v(222.41, -22.41) * mm, "end": v(223, -21) * mm});
            skArc(sketch, "E124.2.0.97", {"start": v(177, -20.53) * mm, "mid": v(176.59, -19.3) * mm, "end": v(175.52, -18.6) * mm});
            skLineSegment(sketch, "E124.2.0.98", {"start": v(179, 23) * mm, "end": v(179.47, 23) * mm});
            skLineSegment(sketch, "E124.2.0.99", {"start": v(220.25, -19.25) * mm, "end": v(220.25, -7.4) * mm});
            skArc(sketch, "E124.2.0.100", {"start": v(184.2, 24.26) * mm, "mid": v(184.36, 23.4) * mm, "end": v(185.16, 23) * mm});
            skLineSegment(sketch, "E124.2.0.101", {"start": v(207.4, -20.25) * mm, "end": v(219.25, -20.25) * mm});
            skLineSegment(sketch, "E124.2.0.102", {"start": v(223, 21) * mm, "end": v(223, 20.53) * mm});
            skLineSegment(sketch, "E124.2.0.103", {"start": v(190.73, -23) * mm, "end": v(185.16, -23) * mm});
            skLineSegment(sketch, "E124.2.0.104", {"start": v(175.74, -15.8) * mm, "end": v(156.57, -10.67) * mm});
            skArc(sketch, "E124.2.0.105", {"start": v(179.7, 7.07) * mm, "mid": v(178.5, 0) * mm, "end": v(179.7, -7.07) * mm});
            skArc(sketch, "E124.2.0.106", {"start": v(223, 9.27) * mm, "mid": v(223.02, 9.06) * mm, "end": v(223.09, 8.86) * mm});
            skArc(sketch, "E124.2.0.107", {"start": v(181.4, -24.48) * mm, "mid": v(180.7, -23.41) * mm, "end": v(179.47, -23) * mm});
            skLineSegment(sketch, "E124.2.0.108", {"start": v(223, -20.53) * mm, "end": v(223, -21) * mm});
            skArc(sketch, "E124.2.0.109", {"start": v(179.47, 23) * mm, "mid": v(180.7, 23.41) * mm, "end": v(181.4, 24.48) * mm});
            skArc(sketch, "E124.2.0.110", {"start": v(177, -9.27) * mm, "mid": v(176.98, -9.06) * mm, "end": v(176.91, -8.86) * mm});
            skLineSegment(sketch, "E124.2.0.111", {"start": v(223, -14.84) * mm, "end": v(223, -9.27) * mm});
            skLineSegment(sketch, "E124.2.0.112", {"start": v(220.53, 23) * mm, "end": v(221, 23) * mm});
            skArc(sketch, "E124.2.0.113", {"start": v(175.52, 18.6) * mm, "mid": v(176.59, 19.3) * mm, "end": v(177, 20.53) * mm});
            skArc(sketch, "E124.2.0.114", {"start": v(185.16, -23) * mm, "mid": v(184.36, -23.4) * mm, "end": v(184.2, -24.26) * mm});
            skArc(sketch, "E124.2.0.115", {"start": v(175.74, -15.8) * mm, "mid": v(176.6, -15.64) * mm, "end": v(177, -14.84) * mm});
            skArc(sketch, "E124.2.0.116", {"start": v(224.48, -18.6) * mm, "mid": v(223.41, -19.3) * mm, "end": v(223, -20.53) * mm});
            skLineSegment(sketch, "E124.2.0.117", {"start": v(179.75, 19.25) * mm, "end": v(179.75, 7.4) * mm});
            skArc(sketch, "E124.2.0.118", {"start": v(179.75, -19.25) * mm, "mid": v(180.04, -19.96) * mm, "end": v(180.75, -20.25) * mm});
            skArc(sketch, "E124.2.0.119", {"start": v(223, 21) * mm, "mid": v(222.41, 22.41) * mm, "end": v(221, 23) * mm});
            skArc(sketch, "E124.2.0.120", {"start": v(224.26, 15.8) * mm, "mid": v(223.4, 15.64) * mm, "end": v(223, 14.84) * mm});
            skArc(sketch, "E124.2.0.121", {"start": v(177, 14.84) * mm, "mid": v(176.6, 15.64) * mm, "end": v(175.74, 15.8) * mm});
            skArc(sketch, "E124.2.0.122", {"start": v(179.7, 7.07) * mm, "mid": v(179.74, 7.23) * mm, "end": v(179.75, 7.4) * mm});
            skLineSegment(sketch, "E124.2.0.123", {"start": v(177, 20.53) * mm, "end": v(177, 21) * mm});
            skArc(sketch, "E124.3.0.0", {"start": v(345, 39) * mm, "mid": v(343.24, 43.24) * mm, "end": v(339, 45) * mm});
            skLineSegment(sketch, "E124.3.0.1", {"start": v(255, -11.88) * mm, "end": v(255, -39) * mm});
            skLineSegment(sketch, "E124.3.0.2", {"start": v(345, 11.88) * mm, "end": v(345, 39) * mm});
            skArc(sketch, "E124.3.0.3", {"start": v(255, -39) * mm, "mid": v(256.76, -43.24) * mm, "end": v(261, -45) * mm});
            skLineSegment(sketch, "E124.3.0.4", {"start": v(257.75, -16.44) * mm, "end": v(257.75, -39) * mm});
            skLineSegment(sketch, "E124.3.0.5", {"start": v(261, -45) * mm, "end": v(339, -45) * mm});
            skArc(sketch, "E124.3.0.6", {"start": v(257.75, -39) * mm, "mid": v(258.7, -41.3) * mm, "end": v(261, -42.25) * mm});
            skLineSegment(sketch, "E124.3.0.7", {"start": v(255, 39) * mm, "end": v(255, 11.88) * mm});
            skArc(sketch, "E124.3.0.8", {"start": v(261, 42.25) * mm, "mid": v(258.7, 41.3) * mm, "end": v(257.75, 39) * mm});
            skArc(sketch, "E124.3.0.9", {"start": v(261, 45) * mm, "mid": v(256.76, 43.24) * mm, "end": v(255, 39) * mm});
            skLineSegment(sketch, "E124.3.0.10", {"start": v(257.75, 39) * mm, "end": v(257.75, 16.44) * mm});
            skArc(sketch, "E124.3.0.11", {"start": v(342.25, 39) * mm, "mid": v(341.3, 41.3) * mm, "end": v(339, 42.25) * mm});
            skLineSegment(sketch, "E124.3.0.12", {"start": v(339, 45) * mm, "end": v(261, 45) * mm});
            skLineSegment(sketch, "E124.3.0.13", {"start": v(342.25, 16.44) * mm, "end": v(342.25, 39) * mm});
            skLineSegment(sketch, "E124.3.0.14", {"start": v(310.99, 42.25) * mm, "end": v(289.01, 42.25) * mm});
            skArc(sketch, "E124.3.0.15", {"start": v(285.5, 39.73) * mm, "mid": v(285.15, 41.47) * mm, "end": v(283.56, 42.25) * mm});
            skLineSegment(sketch, "E124.3.0.16", {"start": v(339, 42.25) * mm, "end": v(316.44, 42.25) * mm});
            skLineSegment(sketch, "E124.3.0.17", {"start": v(324.26, 15.8) * mm, "end": v(343.43, 10.67) * mm});
            skArc(sketch, "E124.3.0.18", {"start": v(339.73, 14.5) * mm, "mid": v(341.47, 14.85) * mm, "end": v(342.25, 16.44) * mm});
            skLineSegment(sketch, "E124.3.0.19", {"start": v(283.56, 42.25) * mm, "end": v(261, 42.25) * mm});
            skArc(sketch, "E124.3.0.20", {"start": v(291.14, -23.09) * mm, "mid": v(300, -25) * mm, "end": v(308.86, -23.09) * mm});
            skLineSegment(sketch, "E124.3.0.21", {"start": v(260.27, 14.5) * mm, "end": v(275.52, 18.6) * mm});
            skArc(sketch, "E124.3.0.22", {"start": v(257.75, 16.44) * mm, "mid": v(258.53, 14.85) * mm, "end": v(260.27, 14.5) * mm});
            skArc(sketch, "E124.3.0.23", {"start": v(308.86, 23.09) * mm, "mid": v(309.06, 23.02) * mm, "end": v(309.27, 23) * mm});
            skArc(sketch, "E124.3.0.24", {"start": v(320.25, 7.4) * mm, "mid": v(320.26, 7.23) * mm, "end": v(320.3, 7.07) * mm});
            skArc(sketch, "E124.3.0.25", {"start": v(314.5, -39.73) * mm, "mid": v(314.85, -41.47) * mm, "end": v(316.44, -42.25) * mm});
            skArc(sketch, "E124.3.0.26", {"start": v(320.53, -23) * mm, "mid": v(319.3, -23.41) * mm, "end": v(318.6, -24.48) * mm});
            skArc(sketch, "E124.3.0.27", {"start": v(279.75, -7.4) * mm, "mid": v(279.74, -7.23) * mm, "end": v(279.7, -7.07) * mm});
            skArc(sketch, "E124.3.0.28", {"start": v(339, -42.25) * mm, "mid": v(341.3, -41.3) * mm, "end": v(342.25, -39) * mm});
            skLineSegment(sketch, "E124.3.0.29", {"start": v(316.44, -42.25) * mm, "end": v(339, -42.25) * mm});
            skArc(sketch, "E124.3.0.30", {"start": v(345, -11.88) * mm, "mid": v(344.51, -10.89) * mm, "end": v(343.43, -10.67) * mm});
            skArc(sketch, "E124.3.0.31", {"start": v(283.56, -42.25) * mm, "mid": v(285.15, -41.47) * mm, "end": v(285.5, -39.73) * mm});
            skArc(sketch, "E124.3.0.32", {"start": v(255, 11.88) * mm, "mid": v(255.49, 10.89) * mm, "end": v(256.57, 10.67) * mm});
            skLineSegment(sketch, "E124.3.0.33", {"start": v(280.75, -20.25) * mm, "end": v(292.6, -20.25) * mm});
            skArc(sketch, "E124.3.0.34", {"start": v(308.86, 23.09) * mm, "mid": v(300, 25) * mm, "end": v(291.14, 23.09) * mm});
            skArc(sketch, "E124.3.0.35", {"start": v(339, -45) * mm, "mid": v(343.24, -43.24) * mm, "end": v(345, -39) * mm});
            skLineSegment(sketch, "E124.3.0.36", {"start": v(339.73, -14.5) * mm, "end": v(324.48, -18.6) * mm});
            skLineSegment(sketch, "E124.3.0.37", {"start": v(324.48, 18.6) * mm, "end": v(339.73, 14.5) * mm});
            skArc(sketch, "E124.3.0.38", {"start": v(320.3, -7.07) * mm, "mid": v(320.26, -7.23) * mm, "end": v(320.25, -7.4) * mm});
            skArc(sketch, "E124.3.0.39", {"start": v(316.44, 42.25) * mm, "mid": v(314.85, 41.47) * mm, "end": v(314.5, 39.73) * mm});
            skArc(sketch, "E124.3.0.40", {"start": v(323.09, -8.86) * mm, "mid": v(325, 0) * mm, "end": v(323.09, 8.86) * mm});
            skArc(sketch, "E124.3.0.41", {"start": v(318.6, 24.48) * mm, "mid": v(319.3, 23.41) * mm, "end": v(320.53, 23) * mm});
            skArc(sketch, "E124.3.0.42", {"start": v(256.57, -10.67) * mm, "mid": v(255.49, -10.89) * mm, "end": v(255, -11.88) * mm});
            skLineSegment(sketch, "E124.3.0.43", {"start": v(277, -21) * mm, "end": v(277, -20.53) * mm});
            skLineSegment(sketch, "E124.3.0.44", {"start": v(261, -42.25) * mm, "end": v(283.56, -42.25) * mm});
            skLineSegment(sketch, "E124.3.0.45", {"start": v(285.16, 23) * mm, "end": v(290.73, 23) * mm});
            skLineSegment(sketch, "E124.3.0.46", {"start": v(292.6, 20.25) * mm, "end": v(280.75, 20.25) * mm});
            skLineSegment(sketch, "E124.3.0.47", {"start": v(345, -39) * mm, "end": v(345, -11.88) * mm});
            skLineSegment(sketch, "E124.3.0.48", {"start": v(289.01, -42.25) * mm, "end": v(310.99, -42.25) * mm});
            skLineSegment(sketch, "E124.3.0.49", {"start": v(289.01, 42.25) * mm, "end": v(284.2, 24.26) * mm});
            skLineSegment(sketch, "E124.3.0.50", {"start": v(277, 14.84) * mm, "end": v(277, 9.27) * mm});
            skArc(sketch, "E124.3.0.51", {"start": v(320.25, 19.25) * mm, "mid": v(319.96, 19.96) * mm, "end": v(319.25, 20.25) * mm});
            skArc(sketch, "E124.3.0.52", {"start": v(292.93, -20.3) * mm, "mid": v(300, -21.5) * mm, "end": v(307.07, -20.3) * mm});
            skArc(sketch, "E124.3.0.53", {"start": v(307.07, 20.3) * mm, "mid": v(300, 21.5) * mm, "end": v(292.93, 20.3) * mm});
            skArc(sketch, "E124.3.0.54", {"start": v(277, -21) * mm, "mid": v(277.59, -22.41) * mm, "end": v(279, -23) * mm});
            skLineSegment(sketch, "E124.3.0.55", {"start": v(281.4, 24.48) * mm, "end": v(285.5, 39.73) * mm});
            skArc(sketch, "E124.3.0.56", {"start": v(307.4, -20.25) * mm, "mid": v(307.23, -20.26) * mm, "end": v(307.07, -20.3) * mm});
            skLineSegment(sketch, "E124.3.0.57", {"start": v(319.25, 20.25) * mm, "end": v(307.4, 20.25) * mm});
            skArc(sketch, "E124.3.0.58", {"start": v(276.91, 8.86) * mm, "mid": v(276.98, 9.06) * mm, "end": v(277, 9.27) * mm});
            skArc(sketch, "E124.3.0.59", {"start": v(319.25, -20.25) * mm, "mid": v(319.96, -19.96) * mm, "end": v(320.25, -19.25) * mm});
            skArc(sketch, "E124.3.0.60", {"start": v(323.09, -8.86) * mm, "mid": v(323.02, -9.06) * mm, "end": v(323, -9.27) * mm});
            skLineSegment(sketch, "E124.3.0.61", {"start": v(314.5, 39.73) * mm, "end": v(318.6, 24.48) * mm});
            skArc(sketch, "E124.3.0.62", {"start": v(280.75, 20.25) * mm, "mid": v(280.04, 19.96) * mm, "end": v(279.75, 19.25) * mm});
            skLineSegment(sketch, "E124.3.0.63", {"start": v(256.57, 10.67) * mm, "end": v(275.74, 15.8) * mm});
            skLineSegment(sketch, "E124.3.0.64", {"start": v(320.25, 7.4) * mm, "end": v(320.25, 19.25) * mm});
            skLineSegment(sketch, "E124.3.0.65", {"start": v(342.25, -39) * mm, "end": v(342.25, -16.44) * mm});
            skArc(sketch, "E124.3.0.66", {"start": v(291.14, -23.09) * mm, "mid": v(290.94, -23.02) * mm, "end": v(290.73, -23) * mm});
            skArc(sketch, "E124.3.0.67", {"start": v(320.3, -7.07) * mm, "mid": v(321.5, 0) * mm, "end": v(320.3, 7.07) * mm});
            skArc(sketch, "E124.3.0.68", {"start": v(260.27, -14.5) * mm, "mid": v(258.53, -14.85) * mm, "end": v(257.75, -16.44) * mm});
            skArc(sketch, "E124.3.0.69", {"start": v(343.43, 10.67) * mm, "mid": v(344.51, 10.89) * mm, "end": v(345, 11.88) * mm});
            skArc(sketch, "E124.3.0.70", {"start": v(290.73, 23) * mm, "mid": v(290.94, 23.02) * mm, "end": v(291.14, 23.09) * mm});
            skLineSegment(sketch, "E124.3.0.71", {"start": v(343.43, -10.67) * mm, "end": v(324.26, -15.8) * mm});
            skLineSegment(sketch, "E124.3.0.72", {"start": v(314.84, -23) * mm, "end": v(309.27, -23) * mm});
            skLineSegment(sketch, "E124.3.0.73", {"start": v(285.5, -39.73) * mm, "end": v(281.4, -24.48) * mm});
            skLineSegment(sketch, "E124.3.0.74", {"start": v(310.99, -42.25) * mm, "end": v(315.8, -24.26) * mm});
            skLineSegment(sketch, "E124.3.0.75", {"start": v(279.75, -7.4) * mm, "end": v(279.75, -19.25) * mm});
            skLineSegment(sketch, "E124.3.0.76", {"start": v(277, -9.27) * mm, "end": v(277, -14.84) * mm});
            skLineSegment(sketch, "E124.3.0.77", {"start": v(321, -23) * mm, "end": v(320.53, -23) * mm});
            skArc(sketch, "E124.3.0.78", {"start": v(315.8, -24.26) * mm, "mid": v(315.64, -23.4) * mm, "end": v(314.84, -23) * mm});
            skArc(sketch, "E124.3.0.79", {"start": v(314.84, 23) * mm, "mid": v(315.64, 23.4) * mm, "end": v(315.8, 24.26) * mm});
            skArc(sketch, "E124.3.0.80", {"start": v(279, 23) * mm, "mid": v(277.59, 22.41) * mm, "end": v(277, 21) * mm});
            skLineSegment(sketch, "E124.3.0.81", {"start": v(318.6, -24.48) * mm, "end": v(314.5, -39.73) * mm});
            skArc(sketch, "E124.3.0.82", {"start": v(276.91, 8.86) * mm, "mid": v(275, 0) * mm, "end": v(276.91, -8.86) * mm});
            skArc(sketch, "E124.3.0.83", {"start": v(323, -14.84) * mm, "mid": v(323.4, -15.64) * mm, "end": v(324.26, -15.8) * mm});
            skArc(sketch, "E124.3.0.84", {"start": v(292.6, 20.25) * mm, "mid": v(292.77, 20.26) * mm, "end": v(292.93, 20.3) * mm});
            skLineSegment(sketch, "E124.3.0.85", {"start": v(279.47, -23) * mm, "end": v(279, -23) * mm});
            skLineSegment(sketch, "E124.3.0.86", {"start": v(315.8, 24.26) * mm, "end": v(310.99, 42.25) * mm});
            skArc(sketch, "E124.3.0.87", {"start": v(323, 20.53) * mm, "mid": v(323.41, 19.3) * mm, "end": v(324.48, 18.6) * mm});
            skArc(sketch, "E124.3.0.88", {"start": v(309.27, -23) * mm, "mid": v(309.06, -23.02) * mm, "end": v(308.86, -23.09) * mm});
            skLineSegment(sketch, "E124.3.0.89", {"start": v(284.2, -24.26) * mm, "end": v(289.01, -42.25) * mm});
            skArc(sketch, "E124.3.0.90", {"start": v(292.93, -20.3) * mm, "mid": v(292.77, -20.26) * mm, "end": v(292.6, -20.25) * mm});
            skArc(sketch, "E124.3.0.91", {"start": v(342.25, -16.44) * mm, "mid": v(341.47, -14.85) * mm, "end": v(339.73, -14.5) * mm});
            skLineSegment(sketch, "E124.3.0.92", {"start": v(275.52, -18.6) * mm, "end": v(260.27, -14.5) * mm});
            skLineSegment(sketch, "E124.3.0.93", {"start": v(323, 9.27) * mm, "end": v(323, 14.84) * mm});
            skArc(sketch, "E124.3.0.94", {"start": v(307.07, 20.3) * mm, "mid": v(307.23, 20.26) * mm, "end": v(307.4, 20.25) * mm});
            skLineSegment(sketch, "E124.3.0.95", {"start": v(309.27, 23) * mm, "end": v(314.84, 23) * mm});
            skArc(sketch, "E124.3.0.96", {"start": v(321, -23) * mm, "mid": v(322.41, -22.41) * mm, "end": v(323, -21) * mm});
            skArc(sketch, "E124.3.0.97", {"start": v(277, -20.53) * mm, "mid": v(276.59, -19.3) * mm, "end": v(275.52, -18.6) * mm});
            skLineSegment(sketch, "E124.3.0.98", {"start": v(279, 23) * mm, "end": v(279.47, 23) * mm});
            skLineSegment(sketch, "E124.3.0.99", {"start": v(320.25, -19.25) * mm, "end": v(320.25, -7.4) * mm});
            skArc(sketch, "E124.3.0.100", {"start": v(284.2, 24.26) * mm, "mid": v(284.36, 23.4) * mm, "end": v(285.16, 23) * mm});
            skLineSegment(sketch, "E124.3.0.101", {"start": v(307.4, -20.25) * mm, "end": v(319.25, -20.25) * mm});
            skLineSegment(sketch, "E124.3.0.102", {"start": v(323, 21) * mm, "end": v(323, 20.53) * mm});
            skLineSegment(sketch, "E124.3.0.103", {"start": v(290.73, -23) * mm, "end": v(285.16, -23) * mm});
            skLineSegment(sketch, "E124.3.0.104", {"start": v(275.74, -15.8) * mm, "end": v(256.57, -10.67) * mm});
            skArc(sketch, "E124.3.0.105", {"start": v(279.7, 7.07) * mm, "mid": v(278.5, 0) * mm, "end": v(279.7, -7.07) * mm});
            skArc(sketch, "E124.3.0.106", {"start": v(323, 9.27) * mm, "mid": v(323.02, 9.06) * mm, "end": v(323.09, 8.86) * mm});
            skArc(sketch, "E124.3.0.107", {"start": v(281.4, -24.48) * mm, "mid": v(280.7, -23.41) * mm, "end": v(279.47, -23) * mm});
            skLineSegment(sketch, "E124.3.0.108", {"start": v(323, -20.53) * mm, "end": v(323, -21) * mm});
            skArc(sketch, "E124.3.0.109", {"start": v(279.47, 23) * mm, "mid": v(280.7, 23.41) * mm, "end": v(281.4, 24.48) * mm});
            skArc(sketch, "E124.3.0.110", {"start": v(277, -9.27) * mm, "mid": v(276.98, -9.06) * mm, "end": v(276.91, -8.86) * mm});
            skLineSegment(sketch, "E124.3.0.111", {"start": v(323, -14.84) * mm, "end": v(323, -9.27) * mm});
            skLineSegment(sketch, "E124.3.0.112", {"start": v(320.53, 23) * mm, "end": v(321, 23) * mm});
            skArc(sketch, "E124.3.0.113", {"start": v(275.52, 18.6) * mm, "mid": v(276.59, 19.3) * mm, "end": v(277, 20.53) * mm});
            skArc(sketch, "E124.3.0.114", {"start": v(285.16, -23) * mm, "mid": v(284.36, -23.4) * mm, "end": v(284.2, -24.26) * mm});
            skArc(sketch, "E124.3.0.115", {"start": v(275.74, -15.8) * mm, "mid": v(276.6, -15.64) * mm, "end": v(277, -14.84) * mm});
            skArc(sketch, "E124.3.0.116", {"start": v(324.48, -18.6) * mm, "mid": v(323.41, -19.3) * mm, "end": v(323, -20.53) * mm});
            skLineSegment(sketch, "E124.3.0.117", {"start": v(279.75, 19.25) * mm, "end": v(279.75, 7.4) * mm});
            skArc(sketch, "E124.3.0.118", {"start": v(279.75, -19.25) * mm, "mid": v(280.04, -19.96) * mm, "end": v(280.75, -20.25) * mm});
            skArc(sketch, "E124.3.0.119", {"start": v(323, 21) * mm, "mid": v(322.41, 22.41) * mm, "end": v(321, 23) * mm});
            skArc(sketch, "E124.3.0.120", {"start": v(324.26, 15.8) * mm, "mid": v(323.4, 15.64) * mm, "end": v(323, 14.84) * mm});
            skArc(sketch, "E124.3.0.121", {"start": v(277, 14.84) * mm, "mid": v(276.6, 15.64) * mm, "end": v(275.74, 15.8) * mm});
            skArc(sketch, "E124.3.0.122", {"start": v(279.7, 7.07) * mm, "mid": v(279.74, 7.23) * mm, "end": v(279.75, 7.4) * mm});
            skLineSegment(sketch, "E124.3.0.123", {"start": v(277, 20.53) * mm, "end": v(277, 21) * mm});
            skArc(sketch, "E124.4.0.0", {"start": v(445, 39) * mm, "mid": v(443.24, 43.24) * mm, "end": v(439, 45) * mm});
            skLineSegment(sketch, "E124.4.0.1", {"start": v(355, -11.88) * mm, "end": v(355, -39) * mm});
            skLineSegment(sketch, "E124.4.0.2", {"start": v(445, 11.88) * mm, "end": v(445, 39) * mm});
            skArc(sketch, "E124.4.0.3", {"start": v(355, -39) * mm, "mid": v(356.76, -43.24) * mm, "end": v(361, -45) * mm});
            skLineSegment(sketch, "E124.4.0.4", {"start": v(357.75, -16.44) * mm, "end": v(357.75, -39) * mm});
            skLineSegment(sketch, "E124.4.0.5", {"start": v(361, -45) * mm, "end": v(439, -45) * mm});
            skArc(sketch, "E124.4.0.6", {"start": v(357.75, -39) * mm, "mid": v(358.7, -41.3) * mm, "end": v(361, -42.25) * mm});
            skLineSegment(sketch, "E124.4.0.7", {"start": v(355, 39) * mm, "end": v(355, 11.88) * mm});
            skArc(sketch, "E124.4.0.8", {"start": v(361, 42.25) * mm, "mid": v(358.7, 41.3) * mm, "end": v(357.75, 39) * mm});
            skArc(sketch, "E124.4.0.9", {"start": v(361, 45) * mm, "mid": v(356.76, 43.24) * mm, "end": v(355, 39) * mm});
            skLineSegment(sketch, "E124.4.0.10", {"start": v(357.75, 39) * mm, "end": v(357.75, 16.44) * mm});
            skArc(sketch, "E124.4.0.11", {"start": v(442.25, 39) * mm, "mid": v(441.3, 41.3) * mm, "end": v(439, 42.25) * mm});
            skLineSegment(sketch, "E124.4.0.12", {"start": v(439, 45) * mm, "end": v(361, 45) * mm});
            skLineSegment(sketch, "E124.4.0.13", {"start": v(442.25, 16.44) * mm, "end": v(442.25, 39) * mm});
            skLineSegment(sketch, "E124.4.0.14", {"start": v(410.99, 42.25) * mm, "end": v(389.01, 42.25) * mm});
            skArc(sketch, "E124.4.0.15", {"start": v(385.5, 39.73) * mm, "mid": v(385.15, 41.47) * mm, "end": v(383.56, 42.25) * mm});
            skLineSegment(sketch, "E124.4.0.16", {"start": v(439, 42.25) * mm, "end": v(416.44, 42.25) * mm});
            skLineSegment(sketch, "E124.4.0.17", {"start": v(424.26, 15.8) * mm, "end": v(443.43, 10.67) * mm});
            skArc(sketch, "E124.4.0.18", {"start": v(439.73, 14.5) * mm, "mid": v(441.47, 14.85) * mm, "end": v(442.25, 16.44) * mm});
            skLineSegment(sketch, "E124.4.0.19", {"start": v(383.56, 42.25) * mm, "end": v(361, 42.25) * mm});
            skArc(sketch, "E124.4.0.20", {"start": v(391.14, -23.09) * mm, "mid": v(400, -25) * mm, "end": v(408.86, -23.09) * mm});
            skLineSegment(sketch, "E124.4.0.21", {"start": v(360.27, 14.5) * mm, "end": v(375.52, 18.6) * mm});
            skArc(sketch, "E124.4.0.22", {"start": v(357.75, 16.44) * mm, "mid": v(358.53, 14.85) * mm, "end": v(360.27, 14.5) * mm});
            skArc(sketch, "E124.4.0.23", {"start": v(408.86, 23.09) * mm, "mid": v(409.06, 23.02) * mm, "end": v(409.27, 23) * mm});
            skArc(sketch, "E124.4.0.24", {"start": v(420.25, 7.4) * mm, "mid": v(420.26, 7.23) * mm, "end": v(420.3, 7.07) * mm});
            skArc(sketch, "E124.4.0.25", {"start": v(414.5, -39.73) * mm, "mid": v(414.85, -41.47) * mm, "end": v(416.44, -42.25) * mm});
            skArc(sketch, "E124.4.0.26", {"start": v(420.53, -23) * mm, "mid": v(419.3, -23.41) * mm, "end": v(418.6, -24.48) * mm});
            skArc(sketch, "E124.4.0.27", {"start": v(379.75, -7.4) * mm, "mid": v(379.74, -7.23) * mm, "end": v(379.7, -7.07) * mm});
            skArc(sketch, "E124.4.0.28", {"start": v(439, -42.25) * mm, "mid": v(441.3, -41.3) * mm, "end": v(442.25, -39) * mm});
            skLineSegment(sketch, "E124.4.0.29", {"start": v(416.44, -42.25) * mm, "end": v(439, -42.25) * mm});
            skArc(sketch, "E124.4.0.30", {"start": v(445, -11.88) * mm, "mid": v(444.51, -10.89) * mm, "end": v(443.43, -10.67) * mm});
            skArc(sketch, "E124.4.0.31", {"start": v(383.56, -42.25) * mm, "mid": v(385.15, -41.47) * mm, "end": v(385.5, -39.73) * mm});
            skArc(sketch, "E124.4.0.32", {"start": v(355, 11.88) * mm, "mid": v(355.49, 10.89) * mm, "end": v(356.57, 10.67) * mm});
            skLineSegment(sketch, "E124.4.0.33", {"start": v(380.75, -20.25) * mm, "end": v(392.6, -20.25) * mm});
            skArc(sketch, "E124.4.0.34", {"start": v(408.86, 23.09) * mm, "mid": v(400, 25) * mm, "end": v(391.14, 23.09) * mm});
            skArc(sketch, "E124.4.0.35", {"start": v(439, -45) * mm, "mid": v(443.24, -43.24) * mm, "end": v(445, -39) * mm});
            skLineSegment(sketch, "E124.4.0.36", {"start": v(439.73, -14.5) * mm, "end": v(424.48, -18.6) * mm});
            skLineSegment(sketch, "E124.4.0.37", {"start": v(424.48, 18.6) * mm, "end": v(439.73, 14.5) * mm});
            skArc(sketch, "E124.4.0.38", {"start": v(420.3, -7.07) * mm, "mid": v(420.26, -7.23) * mm, "end": v(420.25, -7.4) * mm});
            skArc(sketch, "E124.4.0.39", {"start": v(416.44, 42.25) * mm, "mid": v(414.85, 41.47) * mm, "end": v(414.5, 39.73) * mm});
            skArc(sketch, "E124.4.0.40", {"start": v(423.09, -8.86) * mm, "mid": v(425, 0) * mm, "end": v(423.09, 8.86) * mm});
            skArc(sketch, "E124.4.0.41", {"start": v(418.6, 24.48) * mm, "mid": v(419.3, 23.41) * mm, "end": v(420.53, 23) * mm});
            skArc(sketch, "E124.4.0.42", {"start": v(356.57, -10.67) * mm, "mid": v(355.49, -10.89) * mm, "end": v(355, -11.88) * mm});
            skLineSegment(sketch, "E124.4.0.43", {"start": v(377, -21) * mm, "end": v(377, -20.53) * mm});
            skLineSegment(sketch, "E124.4.0.44", {"start": v(361, -42.25) * mm, "end": v(383.56, -42.25) * mm});
            skLineSegment(sketch, "E124.4.0.45", {"start": v(385.16, 23) * mm, "end": v(390.73, 23) * mm});
            skLineSegment(sketch, "E124.4.0.46", {"start": v(392.6, 20.25) * mm, "end": v(380.75, 20.25) * mm});
            skLineSegment(sketch, "E124.4.0.47", {"start": v(445, -39) * mm, "end": v(445, -11.88) * mm});
            skLineSegment(sketch, "E124.4.0.48", {"start": v(389.01, -42.25) * mm, "end": v(410.99, -42.25) * mm});
            skLineSegment(sketch, "E124.4.0.49", {"start": v(389.01, 42.25) * mm, "end": v(384.2, 24.26) * mm});
            skLineSegment(sketch, "E124.4.0.50", {"start": v(377, 14.84) * mm, "end": v(377, 9.27) * mm});
            skArc(sketch, "E124.4.0.51", {"start": v(420.25, 19.25) * mm, "mid": v(419.96, 19.96) * mm, "end": v(419.25, 20.25) * mm});
            skArc(sketch, "E124.4.0.52", {"start": v(392.93, -20.3) * mm, "mid": v(400, -21.5) * mm, "end": v(407.07, -20.3) * mm});
            skArc(sketch, "E124.4.0.53", {"start": v(407.07, 20.3) * mm, "mid": v(400, 21.5) * mm, "end": v(392.93, 20.3) * mm});
            skArc(sketch, "E124.4.0.54", {"start": v(377, -21) * mm, "mid": v(377.59, -22.41) * mm, "end": v(379, -23) * mm});
            skLineSegment(sketch, "E124.4.0.55", {"start": v(381.4, 24.48) * mm, "end": v(385.5, 39.73) * mm});
            skArc(sketch, "E124.4.0.56", {"start": v(407.4, -20.25) * mm, "mid": v(407.23, -20.26) * mm, "end": v(407.07, -20.3) * mm});
            skLineSegment(sketch, "E124.4.0.57", {"start": v(419.25, 20.25) * mm, "end": v(407.4, 20.25) * mm});
            skArc(sketch, "E124.4.0.58", {"start": v(376.91, 8.86) * mm, "mid": v(376.98, 9.06) * mm, "end": v(377, 9.27) * mm});
            skArc(sketch, "E124.4.0.59", {"start": v(419.25, -20.25) * mm, "mid": v(419.96, -19.96) * mm, "end": v(420.25, -19.25) * mm});
            skArc(sketch, "E124.4.0.60", {"start": v(423.09, -8.86) * mm, "mid": v(423.02, -9.06) * mm, "end": v(423, -9.27) * mm});
            skLineSegment(sketch, "E124.4.0.61", {"start": v(414.5, 39.73) * mm, "end": v(418.6, 24.48) * mm});
            skArc(sketch, "E124.4.0.62", {"start": v(380.75, 20.25) * mm, "mid": v(380.04, 19.96) * mm, "end": v(379.75, 19.25) * mm});
            skLineSegment(sketch, "E124.4.0.63", {"start": v(356.57, 10.67) * mm, "end": v(375.74, 15.8) * mm});
            skLineSegment(sketch, "E124.4.0.64", {"start": v(420.25, 7.4) * mm, "end": v(420.25, 19.25) * mm});
            skLineSegment(sketch, "E124.4.0.65", {"start": v(442.25, -39) * mm, "end": v(442.25, -16.44) * mm});
            skArc(sketch, "E124.4.0.66", {"start": v(391.14, -23.09) * mm, "mid": v(390.94, -23.02) * mm, "end": v(390.73, -23) * mm});
            skArc(sketch, "E124.4.0.67", {"start": v(420.3, -7.07) * mm, "mid": v(421.5, 0) * mm, "end": v(420.3, 7.07) * mm});
            skArc(sketch, "E124.4.0.68", {"start": v(360.27, -14.5) * mm, "mid": v(358.53, -14.85) * mm, "end": v(357.75, -16.44) * mm});
            skArc(sketch, "E124.4.0.69", {"start": v(443.43, 10.67) * mm, "mid": v(444.51, 10.89) * mm, "end": v(445, 11.88) * mm});
            skArc(sketch, "E124.4.0.70", {"start": v(390.73, 23) * mm, "mid": v(390.94, 23.02) * mm, "end": v(391.14, 23.09) * mm});
            skLineSegment(sketch, "E124.4.0.71", {"start": v(443.43, -10.67) * mm, "end": v(424.26, -15.8) * mm});
            skLineSegment(sketch, "E124.4.0.72", {"start": v(414.84, -23) * mm, "end": v(409.27, -23) * mm});
            skLineSegment(sketch, "E124.4.0.73", {"start": v(385.5, -39.73) * mm, "end": v(381.4, -24.48) * mm});
            skLineSegment(sketch, "E124.4.0.74", {"start": v(410.99, -42.25) * mm, "end": v(415.8, -24.26) * mm});
            skLineSegment(sketch, "E124.4.0.75", {"start": v(379.75, -7.4) * mm, "end": v(379.75, -19.25) * mm});
            skLineSegment(sketch, "E124.4.0.76", {"start": v(377, -9.27) * mm, "end": v(377, -14.84) * mm});
            skLineSegment(sketch, "E124.4.0.77", {"start": v(421, -23) * mm, "end": v(420.53, -23) * mm});
            skArc(sketch, "E124.4.0.78", {"start": v(415.8, -24.26) * mm, "mid": v(415.64, -23.4) * mm, "end": v(414.84, -23) * mm});
            skArc(sketch, "E124.4.0.79", {"start": v(414.84, 23) * mm, "mid": v(415.64, 23.4) * mm, "end": v(415.8, 24.26) * mm});
            skArc(sketch, "E124.4.0.80", {"start": v(379, 23) * mm, "mid": v(377.59, 22.41) * mm, "end": v(377, 21) * mm});
            skLineSegment(sketch, "E124.4.0.81", {"start": v(418.6, -24.48) * mm, "end": v(414.5, -39.73) * mm});
            skArc(sketch, "E124.4.0.82", {"start": v(376.91, 8.86) * mm, "mid": v(375, 0) * mm, "end": v(376.91, -8.86) * mm});
            skArc(sketch, "E124.4.0.83", {"start": v(423, -14.84) * mm, "mid": v(423.4, -15.64) * mm, "end": v(424.26, -15.8) * mm});
            skArc(sketch, "E124.4.0.84", {"start": v(392.6, 20.25) * mm, "mid": v(392.77, 20.26) * mm, "end": v(392.93, 20.3) * mm});
            skLineSegment(sketch, "E124.4.0.85", {"start": v(379.47, -23) * mm, "end": v(379, -23) * mm});
            skLineSegment(sketch, "E124.4.0.86", {"start": v(415.8, 24.26) * mm, "end": v(410.99, 42.25) * mm});
            skArc(sketch, "E124.4.0.87", {"start": v(423, 20.53) * mm, "mid": v(423.41, 19.3) * mm, "end": v(424.48, 18.6) * mm});
            skArc(sketch, "E124.4.0.88", {"start": v(409.27, -23) * mm, "mid": v(409.06, -23.02) * mm, "end": v(408.86, -23.09) * mm});
            skLineSegment(sketch, "E124.4.0.89", {"start": v(384.2, -24.26) * mm, "end": v(389.01, -42.25) * mm});
            skArc(sketch, "E124.4.0.90", {"start": v(392.93, -20.3) * mm, "mid": v(392.77, -20.26) * mm, "end": v(392.6, -20.25) * mm});
            skArc(sketch, "E124.4.0.91", {"start": v(442.25, -16.44) * mm, "mid": v(441.47, -14.85) * mm, "end": v(439.73, -14.5) * mm});
            skLineSegment(sketch, "E124.4.0.92", {"start": v(375.52, -18.6) * mm, "end": v(360.27, -14.5) * mm});
            skLineSegment(sketch, "E124.4.0.93", {"start": v(423, 9.27) * mm, "end": v(423, 14.84) * mm});
            skArc(sketch, "E124.4.0.94", {"start": v(407.07, 20.3) * mm, "mid": v(407.23, 20.26) * mm, "end": v(407.4, 20.25) * mm});
            skLineSegment(sketch, "E124.4.0.95", {"start": v(409.27, 23) * mm, "end": v(414.84, 23) * mm});
            skArc(sketch, "E124.4.0.96", {"start": v(421, -23) * mm, "mid": v(422.41, -22.41) * mm, "end": v(423, -21) * mm});
            skArc(sketch, "E124.4.0.97", {"start": v(377, -20.53) * mm, "mid": v(376.59, -19.3) * mm, "end": v(375.52, -18.6) * mm});
            skLineSegment(sketch, "E124.4.0.98", {"start": v(379, 23) * mm, "end": v(379.47, 23) * mm});
            skLineSegment(sketch, "E124.4.0.99", {"start": v(420.25, -19.25) * mm, "end": v(420.25, -7.4) * mm});
            skArc(sketch, "E124.4.0.100", {"start": v(384.2, 24.26) * mm, "mid": v(384.36, 23.4) * mm, "end": v(385.16, 23) * mm});
            skLineSegment(sketch, "E124.4.0.101", {"start": v(407.4, -20.25) * mm, "end": v(419.25, -20.25) * mm});
            skLineSegment(sketch, "E124.4.0.102", {"start": v(423, 21) * mm, "end": v(423, 20.53) * mm});
            skLineSegment(sketch, "E124.4.0.103", {"start": v(390.73, -23) * mm, "end": v(385.16, -23) * mm});
            skLineSegment(sketch, "E124.4.0.104", {"start": v(375.74, -15.8) * mm, "end": v(356.57, -10.67) * mm});
            skArc(sketch, "E124.4.0.105", {"start": v(379.7, 7.07) * mm, "mid": v(378.5, 0) * mm, "end": v(379.7, -7.07) * mm});
            skArc(sketch, "E124.4.0.106", {"start": v(423, 9.27) * mm, "mid": v(423.02, 9.06) * mm, "end": v(423.09, 8.86) * mm});
            skArc(sketch, "E124.4.0.107", {"start": v(381.4, -24.48) * mm, "mid": v(380.7, -23.41) * mm, "end": v(379.47, -23) * mm});
            skLineSegment(sketch, "E124.4.0.108", {"start": v(423, -20.53) * mm, "end": v(423, -21) * mm});
            skArc(sketch, "E124.4.0.109", {"start": v(379.47, 23) * mm, "mid": v(380.7, 23.41) * mm, "end": v(381.4, 24.48) * mm});
            skArc(sketch, "E124.4.0.110", {"start": v(377, -9.27) * mm, "mid": v(376.98, -9.06) * mm, "end": v(376.91, -8.86) * mm});
            skLineSegment(sketch, "E124.4.0.111", {"start": v(423, -14.84) * mm, "end": v(423, -9.27) * mm});
            skLineSegment(sketch, "E124.4.0.112", {"start": v(420.53, 23) * mm, "end": v(421, 23) * mm});
            skArc(sketch, "E124.4.0.113", {"start": v(375.52, 18.6) * mm, "mid": v(376.59, 19.3) * mm, "end": v(377, 20.53) * mm});
            skArc(sketch, "E124.4.0.114", {"start": v(385.16, -23) * mm, "mid": v(384.36, -23.4) * mm, "end": v(384.2, -24.26) * mm});
            skArc(sketch, "E124.4.0.115", {"start": v(375.74, -15.8) * mm, "mid": v(376.6, -15.64) * mm, "end": v(377, -14.84) * mm});
            skArc(sketch, "E124.4.0.116", {"start": v(424.48, -18.6) * mm, "mid": v(423.41, -19.3) * mm, "end": v(423, -20.53) * mm});
            skLineSegment(sketch, "E124.4.0.117", {"start": v(379.75, 19.25) * mm, "end": v(379.75, 7.4) * mm});
            skArc(sketch, "E124.4.0.118", {"start": v(379.75, -19.25) * mm, "mid": v(380.04, -19.96) * mm, "end": v(380.75, -20.25) * mm});
            skArc(sketch, "E124.4.0.119", {"start": v(423, 21) * mm, "mid": v(422.41, 22.41) * mm, "end": v(421, 23) * mm});
            skArc(sketch, "E124.4.0.120", {"start": v(424.26, 15.8) * mm, "mid": v(423.4, 15.64) * mm, "end": v(423, 14.84) * mm});
            skArc(sketch, "E124.4.0.121", {"start": v(377, 14.84) * mm, "mid": v(376.6, 15.64) * mm, "end": v(375.74, 15.8) * mm});
            skArc(sketch, "E124.4.0.122", {"start": v(379.7, 7.07) * mm, "mid": v(379.74, 7.23) * mm, "end": v(379.75, 7.4) * mm});
            skLineSegment(sketch, "E124.4.0.123", {"start": v(377, 20.53) * mm, "end": v(377, 21) * mm});
            skArc(sketch, "E124.5.0.0", {"start": v(545, 39) * mm, "mid": v(543.24, 43.24) * mm, "end": v(539, 45) * mm});
            skLineSegment(sketch, "E124.5.0.1", {"start": v(455, -11.88) * mm, "end": v(455, -39) * mm});
            skLineSegment(sketch, "E124.5.0.2", {"start": v(545, 11.88) * mm, "end": v(545, 39) * mm});
            skArc(sketch, "E124.5.0.3", {"start": v(455, -39) * mm, "mid": v(456.76, -43.24) * mm, "end": v(461, -45) * mm});
            skLineSegment(sketch, "E124.5.0.4", {"start": v(457.75, -16.44) * mm, "end": v(457.75, -39) * mm});
            skLineSegment(sketch, "E124.5.0.5", {"start": v(461, -45) * mm, "end": v(539, -45) * mm});
            skArc(sketch, "E124.5.0.6", {"start": v(457.75, -39) * mm, "mid": v(458.7, -41.3) * mm, "end": v(461, -42.25) * mm});
            skLineSegment(sketch, "E124.5.0.7", {"start": v(455, 39) * mm, "end": v(455, 11.88) * mm});
            skArc(sketch, "E124.5.0.8", {"start": v(461, 42.25) * mm, "mid": v(458.7, 41.3) * mm, "end": v(457.75, 39) * mm});
            skArc(sketch, "E124.5.0.9", {"start": v(461, 45) * mm, "mid": v(456.76, 43.24) * mm, "end": v(455, 39) * mm});
            skLineSegment(sketch, "E124.5.0.10", {"start": v(457.75, 39) * mm, "end": v(457.75, 16.44) * mm});
            skArc(sketch, "E124.5.0.11", {"start": v(542.25, 39) * mm, "mid": v(541.3, 41.3) * mm, "end": v(539, 42.25) * mm});
            skLineSegment(sketch, "E124.5.0.12", {"start": v(539, 45) * mm, "end": v(461, 45) * mm});
            skLineSegment(sketch, "E124.5.0.13", {"start": v(542.25, 16.44) * mm, "end": v(542.25, 39) * mm});
            skLineSegment(sketch, "E124.5.0.14", {"start": v(510.99, 42.25) * mm, "end": v(489.01, 42.25) * mm});
            skArc(sketch, "E124.5.0.15", {"start": v(485.5, 39.73) * mm, "mid": v(485.15, 41.47) * mm, "end": v(483.56, 42.25) * mm});
            skLineSegment(sketch, "E124.5.0.16", {"start": v(539, 42.25) * mm, "end": v(516.44, 42.25) * mm});
            skLineSegment(sketch, "E124.5.0.17", {"start": v(524.26, 15.8) * mm, "end": v(543.43, 10.67) * mm});
            skArc(sketch, "E124.5.0.18", {"start": v(539.73, 14.5) * mm, "mid": v(541.47, 14.85) * mm, "end": v(542.25, 16.44) * mm});
            skLineSegment(sketch, "E124.5.0.19", {"start": v(483.56, 42.25) * mm, "end": v(461, 42.25) * mm});
            skArc(sketch, "E124.5.0.20", {"start": v(491.14, -23.09) * mm, "mid": v(500, -25) * mm, "end": v(508.86, -23.09) * mm});
            skLineSegment(sketch, "E124.5.0.21", {"start": v(460.27, 14.5) * mm, "end": v(475.52, 18.6) * mm});
            skArc(sketch, "E124.5.0.22", {"start": v(457.75, 16.44) * mm, "mid": v(458.53, 14.85) * mm, "end": v(460.27, 14.5) * mm});
            skArc(sketch, "E124.5.0.23", {"start": v(508.86, 23.09) * mm, "mid": v(509.06, 23.02) * mm, "end": v(509.27, 23) * mm});
            skArc(sketch, "E124.5.0.24", {"start": v(520.25, 7.4) * mm, "mid": v(520.26, 7.23) * mm, "end": v(520.3, 7.07) * mm});
            skArc(sketch, "E124.5.0.25", {"start": v(514.5, -39.73) * mm, "mid": v(514.85, -41.47) * mm, "end": v(516.44, -42.25) * mm});
            skArc(sketch, "E124.5.0.26", {"start": v(520.53, -23) * mm, "mid": v(519.3, -23.41) * mm, "end": v(518.6, -24.48) * mm});
            skArc(sketch, "E124.5.0.27", {"start": v(479.75, -7.4) * mm, "mid": v(479.74, -7.23) * mm, "end": v(479.7, -7.07) * mm});
            skArc(sketch, "E124.5.0.28", {"start": v(539, -42.25) * mm, "mid": v(541.3, -41.3) * mm, "end": v(542.25, -39) * mm});
            skLineSegment(sketch, "E124.5.0.29", {"start": v(516.44, -42.25) * mm, "end": v(539, -42.25) * mm});
            skArc(sketch, "E124.5.0.30", {"start": v(545, -11.88) * mm, "mid": v(544.51, -10.89) * mm, "end": v(543.43, -10.67) * mm});
            skArc(sketch, "E124.5.0.31", {"start": v(483.56, -42.25) * mm, "mid": v(485.15, -41.47) * mm, "end": v(485.5, -39.73) * mm});
            skArc(sketch, "E124.5.0.32", {"start": v(455, 11.88) * mm, "mid": v(455.49, 10.89) * mm, "end": v(456.57, 10.67) * mm});
            skLineSegment(sketch, "E124.5.0.33", {"start": v(480.75, -20.25) * mm, "end": v(492.6, -20.25) * mm});
            skArc(sketch, "E124.5.0.34", {"start": v(508.86, 23.09) * mm, "mid": v(500, 25) * mm, "end": v(491.14, 23.09) * mm});
            skArc(sketch, "E124.5.0.35", {"start": v(539, -45) * mm, "mid": v(543.24, -43.24) * mm, "end": v(545, -39) * mm});
            skLineSegment(sketch, "E124.5.0.36", {"start": v(539.73, -14.5) * mm, "end": v(524.48, -18.6) * mm});
            skLineSegment(sketch, "E124.5.0.37", {"start": v(524.48, 18.6) * mm, "end": v(539.73, 14.5) * mm});
            skArc(sketch, "E124.5.0.38", {"start": v(520.3, -7.07) * mm, "mid": v(520.26, -7.23) * mm, "end": v(520.25, -7.4) * mm});
            skArc(sketch, "E124.5.0.39", {"start": v(516.44, 42.25) * mm, "mid": v(514.85, 41.47) * mm, "end": v(514.5, 39.73) * mm});
            skArc(sketch, "E124.5.0.40", {"start": v(523.09, -8.86) * mm, "mid": v(525, 0) * mm, "end": v(523.09, 8.86) * mm});
            skArc(sketch, "E124.5.0.41", {"start": v(518.6, 24.48) * mm, "mid": v(519.3, 23.41) * mm, "end": v(520.53, 23) * mm});
            skArc(sketch, "E124.5.0.42", {"start": v(456.57, -10.67) * mm, "mid": v(455.49, -10.89) * mm, "end": v(455, -11.88) * mm});
            skLineSegment(sketch, "E124.5.0.43", {"start": v(477, -21) * mm, "end": v(477, -20.53) * mm});
            skLineSegment(sketch, "E124.5.0.44", {"start": v(461, -42.25) * mm, "end": v(483.56, -42.25) * mm});
            skLineSegment(sketch, "E124.5.0.45", {"start": v(485.16, 23) * mm, "end": v(490.73, 23) * mm});
            skLineSegment(sketch, "E124.5.0.46", {"start": v(492.6, 20.25) * mm, "end": v(480.75, 20.25) * mm});
            skLineSegment(sketch, "E124.5.0.47", {"start": v(545, -39) * mm, "end": v(545, -11.88) * mm});
            skLineSegment(sketch, "E124.5.0.48", {"start": v(489.01, -42.25) * mm, "end": v(510.99, -42.25) * mm});
            skLineSegment(sketch, "E124.5.0.49", {"start": v(489.01, 42.25) * mm, "end": v(484.2, 24.26) * mm});
            skLineSegment(sketch, "E124.5.0.50", {"start": v(477, 14.84) * mm, "end": v(477, 9.27) * mm});
            skArc(sketch, "E124.5.0.51", {"start": v(520.25, 19.25) * mm, "mid": v(519.96, 19.96) * mm, "end": v(519.25, 20.25) * mm});
            skArc(sketch, "E124.5.0.52", {"start": v(492.93, -20.3) * mm, "mid": v(500, -21.5) * mm, "end": v(507.07, -20.3) * mm});
            skArc(sketch, "E124.5.0.53", {"start": v(507.07, 20.3) * mm, "mid": v(500, 21.5) * mm, "end": v(492.93, 20.3) * mm});
            skArc(sketch, "E124.5.0.54", {"start": v(477, -21) * mm, "mid": v(477.59, -22.41) * mm, "end": v(479, -23) * mm});
            skLineSegment(sketch, "E124.5.0.55", {"start": v(481.4, 24.48) * mm, "end": v(485.5, 39.73) * mm});
            skArc(sketch, "E124.5.0.56", {"start": v(507.4, -20.25) * mm, "mid": v(507.23, -20.26) * mm, "end": v(507.07, -20.3) * mm});
            skLineSegment(sketch, "E124.5.0.57", {"start": v(519.25, 20.25) * mm, "end": v(507.4, 20.25) * mm});
            skArc(sketch, "E124.5.0.58", {"start": v(476.91, 8.86) * mm, "mid": v(476.98, 9.06) * mm, "end": v(477, 9.27) * mm});
            skArc(sketch, "E124.5.0.59", {"start": v(519.25, -20.25) * mm, "mid": v(519.96, -19.96) * mm, "end": v(520.25, -19.25) * mm});
            skArc(sketch, "E124.5.0.60", {"start": v(523.09, -8.86) * mm, "mid": v(523.02, -9.06) * mm, "end": v(523, -9.27) * mm});
            skLineSegment(sketch, "E124.5.0.61", {"start": v(514.5, 39.73) * mm, "end": v(518.6, 24.48) * mm});
            skArc(sketch, "E124.5.0.62", {"start": v(480.75, 20.25) * mm, "mid": v(480.04, 19.96) * mm, "end": v(479.75, 19.25) * mm});
            skLineSegment(sketch, "E124.5.0.63", {"start": v(456.57, 10.67) * mm, "end": v(475.74, 15.8) * mm});
            skLineSegment(sketch, "E124.5.0.64", {"start": v(520.25, 7.4) * mm, "end": v(520.25, 19.25) * mm});
            skLineSegment(sketch, "E124.5.0.65", {"start": v(542.25, -39) * mm, "end": v(542.25, -16.44) * mm});
            skArc(sketch, "E124.5.0.66", {"start": v(491.14, -23.09) * mm, "mid": v(490.94, -23.02) * mm, "end": v(490.73, -23) * mm});
            skArc(sketch, "E124.5.0.67", {"start": v(520.3, -7.07) * mm, "mid": v(521.5, 0) * mm, "end": v(520.3, 7.07) * mm});
            skArc(sketch, "E124.5.0.68", {"start": v(460.27, -14.5) * mm, "mid": v(458.53, -14.85) * mm, "end": v(457.75, -16.44) * mm});
            skArc(sketch, "E124.5.0.69", {"start": v(543.43, 10.67) * mm, "mid": v(544.51, 10.89) * mm, "end": v(545, 11.88) * mm});
            skArc(sketch, "E124.5.0.70", {"start": v(490.73, 23) * mm, "mid": v(490.94, 23.02) * mm, "end": v(491.14, 23.09) * mm});
            skLineSegment(sketch, "E124.5.0.71", {"start": v(543.43, -10.67) * mm, "end": v(524.26, -15.8) * mm});
            skLineSegment(sketch, "E124.5.0.72", {"start": v(514.84, -23) * mm, "end": v(509.27, -23) * mm});
            skLineSegment(sketch, "E124.5.0.73", {"start": v(485.5, -39.73) * mm, "end": v(481.4, -24.48) * mm});
            skLineSegment(sketch, "E124.5.0.74", {"start": v(510.99, -42.25) * mm, "end": v(515.8, -24.26) * mm});
            skLineSegment(sketch, "E124.5.0.75", {"start": v(479.75, -7.4) * mm, "end": v(479.75, -19.25) * mm});
            skLineSegment(sketch, "E124.5.0.76", {"start": v(477, -9.27) * mm, "end": v(477, -14.84) * mm});
            skLineSegment(sketch, "E124.5.0.77", {"start": v(521, -23) * mm, "end": v(520.53, -23) * mm});
            skArc(sketch, "E124.5.0.78", {"start": v(515.8, -24.26) * mm, "mid": v(515.64, -23.4) * mm, "end": v(514.84, -23) * mm});
            skArc(sketch, "E124.5.0.79", {"start": v(514.84, 23) * mm, "mid": v(515.64, 23.4) * mm, "end": v(515.8, 24.26) * mm});
            skArc(sketch, "E124.5.0.80", {"start": v(479, 23) * mm, "mid": v(477.59, 22.41) * mm, "end": v(477, 21) * mm});
            skLineSegment(sketch, "E124.5.0.81", {"start": v(518.6, -24.48) * mm, "end": v(514.5, -39.73) * mm});
            skArc(sketch, "E124.5.0.82", {"start": v(476.91, 8.86) * mm, "mid": v(475, 0) * mm, "end": v(476.91, -8.86) * mm});
            skArc(sketch, "E124.5.0.83", {"start": v(523, -14.84) * mm, "mid": v(523.4, -15.64) * mm, "end": v(524.26, -15.8) * mm});
            skArc(sketch, "E124.5.0.84", {"start": v(492.6, 20.25) * mm, "mid": v(492.77, 20.26) * mm, "end": v(492.93, 20.3) * mm});
            skLineSegment(sketch, "E124.5.0.85", {"start": v(479.47, -23) * mm, "end": v(479, -23) * mm});
            skLineSegment(sketch, "E124.5.0.86", {"start": v(515.8, 24.26) * mm, "end": v(510.99, 42.25) * mm});
            skArc(sketch, "E124.5.0.87", {"start": v(523, 20.53) * mm, "mid": v(523.41, 19.3) * mm, "end": v(524.48, 18.6) * mm});
            skArc(sketch, "E124.5.0.88", {"start": v(509.27, -23) * mm, "mid": v(509.06, -23.02) * mm, "end": v(508.86, -23.09) * mm});
            skLineSegment(sketch, "E124.5.0.89", {"start": v(484.2, -24.26) * mm, "end": v(489.01, -42.25) * mm});
            skArc(sketch, "E124.5.0.90", {"start": v(492.93, -20.3) * mm, "mid": v(492.77, -20.26) * mm, "end": v(492.6, -20.25) * mm});
            skArc(sketch, "E124.5.0.91", {"start": v(542.25, -16.44) * mm, "mid": v(541.47, -14.85) * mm, "end": v(539.73, -14.5) * mm});
            skLineSegment(sketch, "E124.5.0.92", {"start": v(475.52, -18.6) * mm, "end": v(460.27, -14.5) * mm});
            skLineSegment(sketch, "E124.5.0.93", {"start": v(523, 9.27) * mm, "end": v(523, 14.84) * mm});
            skArc(sketch, "E124.5.0.94", {"start": v(507.07, 20.3) * mm, "mid": v(507.23, 20.26) * mm, "end": v(507.4, 20.25) * mm});
            skLineSegment(sketch, "E124.5.0.95", {"start": v(509.27, 23) * mm, "end": v(514.84, 23) * mm});
            skArc(sketch, "E124.5.0.96", {"start": v(521, -23) * mm, "mid": v(522.41, -22.41) * mm, "end": v(523, -21) * mm});
            skArc(sketch, "E124.5.0.97", {"start": v(477, -20.53) * mm, "mid": v(476.59, -19.3) * mm, "end": v(475.52, -18.6) * mm});
            skLineSegment(sketch, "E124.5.0.98", {"start": v(479, 23) * mm, "end": v(479.47, 23) * mm});
            skLineSegment(sketch, "E124.5.0.99", {"start": v(520.25, -19.25) * mm, "end": v(520.25, -7.4) * mm});
            skArc(sketch, "E124.5.0.100", {"start": v(484.2, 24.26) * mm, "mid": v(484.36, 23.4) * mm, "end": v(485.16, 23) * mm});
            skLineSegment(sketch, "E124.5.0.101", {"start": v(507.4, -20.25) * mm, "end": v(519.25, -20.25) * mm});
            skLineSegment(sketch, "E124.5.0.102", {"start": v(523, 21) * mm, "end": v(523, 20.53) * mm});
            skLineSegment(sketch, "E124.5.0.103", {"start": v(490.73, -23) * mm, "end": v(485.16, -23) * mm});
            skLineSegment(sketch, "E124.5.0.104", {"start": v(475.74, -15.8) * mm, "end": v(456.57, -10.67) * mm});
            skArc(sketch, "E124.5.0.105", {"start": v(479.7, 7.07) * mm, "mid": v(478.5, 0) * mm, "end": v(479.7, -7.07) * mm});
            skArc(sketch, "E124.5.0.106", {"start": v(523, 9.27) * mm, "mid": v(523.02, 9.06) * mm, "end": v(523.09, 8.86) * mm});
            skArc(sketch, "E124.5.0.107", {"start": v(481.4, -24.48) * mm, "mid": v(480.7, -23.41) * mm, "end": v(479.47, -23) * mm});
            skLineSegment(sketch, "E124.5.0.108", {"start": v(523, -20.53) * mm, "end": v(523, -21) * mm});
            skArc(sketch, "E124.5.0.109", {"start": v(479.47, 23) * mm, "mid": v(480.7, 23.41) * mm, "end": v(481.4, 24.48) * mm});
            skArc(sketch, "E124.5.0.110", {"start": v(477, -9.27) * mm, "mid": v(476.98, -9.06) * mm, "end": v(476.91, -8.86) * mm});
            skLineSegment(sketch, "E124.5.0.111", {"start": v(523, -14.84) * mm, "end": v(523, -9.27) * mm});
            skLineSegment(sketch, "E124.5.0.112", {"start": v(520.53, 23) * mm, "end": v(521, 23) * mm});
            skArc(sketch, "E124.5.0.113", {"start": v(475.52, 18.6) * mm, "mid": v(476.59, 19.3) * mm, "end": v(477, 20.53) * mm});
            skArc(sketch, "E124.5.0.114", {"start": v(485.16, -23) * mm, "mid": v(484.36, -23.4) * mm, "end": v(484.2, -24.26) * mm});
            skArc(sketch, "E124.5.0.115", {"start": v(475.74, -15.8) * mm, "mid": v(476.6, -15.64) * mm, "end": v(477, -14.84) * mm});
            skArc(sketch, "E124.5.0.116", {"start": v(524.48, -18.6) * mm, "mid": v(523.41, -19.3) * mm, "end": v(523, -20.53) * mm});
            skLineSegment(sketch, "E124.5.0.117", {"start": v(479.75, 19.25) * mm, "end": v(479.75, 7.4) * mm});
            skArc(sketch, "E124.5.0.118", {"start": v(479.75, -19.25) * mm, "mid": v(480.04, -19.96) * mm, "end": v(480.75, -20.25) * mm});
            skArc(sketch, "E124.5.0.119", {"start": v(523, 21) * mm, "mid": v(522.41, 22.41) * mm, "end": v(521, 23) * mm});
            skArc(sketch, "E124.5.0.120", {"start": v(524.26, 15.8) * mm, "mid": v(523.4, 15.64) * mm, "end": v(523, 14.84) * mm});
            skArc(sketch, "E124.5.0.121", {"start": v(477, 14.84) * mm, "mid": v(476.6, 15.64) * mm, "end": v(475.74, 15.8) * mm});
            skArc(sketch, "E124.5.0.122", {"start": v(479.7, 7.07) * mm, "mid": v(479.74, 7.23) * mm, "end": v(479.75, 7.4) * mm});
            skLineSegment(sketch, "E124.5.0.123", {"start": v(477, 20.53) * mm, "end": v(477, 21) * mm});
            skArc(sketch, "E124.6.0.0", {"start": v(645, 39) * mm, "mid": v(643.24, 43.24) * mm, "end": v(639, 45) * mm});
            skLineSegment(sketch, "E124.6.0.1", {"start": v(555, -11.88) * mm, "end": v(555, -39) * mm});
            skLineSegment(sketch, "E124.6.0.2", {"start": v(645, 11.88) * mm, "end": v(645, 39) * mm});
            skArc(sketch, "E124.6.0.3", {"start": v(555, -39) * mm, "mid": v(556.76, -43.24) * mm, "end": v(561, -45) * mm});
            skLineSegment(sketch, "E124.6.0.4", {"start": v(557.75, -16.44) * mm, "end": v(557.75, -39) * mm});
            skLineSegment(sketch, "E124.6.0.5", {"start": v(561, -45) * mm, "end": v(639, -45) * mm});
            skArc(sketch, "E124.6.0.6", {"start": v(557.75, -39) * mm, "mid": v(558.7, -41.3) * mm, "end": v(561, -42.25) * mm});
            skLineSegment(sketch, "E124.6.0.7", {"start": v(555, 39) * mm, "end": v(555, 11.88) * mm});
            skArc(sketch, "E124.6.0.8", {"start": v(561, 42.25) * mm, "mid": v(558.7, 41.3) * mm, "end": v(557.75, 39) * mm});
            skArc(sketch, "E124.6.0.9", {"start": v(561, 45) * mm, "mid": v(556.76, 43.24) * mm, "end": v(555, 39) * mm});
            skLineSegment(sketch, "E124.6.0.10", {"start": v(557.75, 39) * mm, "end": v(557.75, 16.44) * mm});
            skArc(sketch, "E124.6.0.11", {"start": v(642.25, 39) * mm, "mid": v(641.3, 41.3) * mm, "end": v(639, 42.25) * mm});
            skLineSegment(sketch, "E124.6.0.12", {"start": v(639, 45) * mm, "end": v(561, 45) * mm});
            skLineSegment(sketch, "E124.6.0.13", {"start": v(642.25, 16.44) * mm, "end": v(642.25, 39) * mm});
            skLineSegment(sketch, "E124.6.0.14", {"start": v(610.99, 42.25) * mm, "end": v(589.01, 42.25) * mm});
            skArc(sketch, "E124.6.0.15", {"start": v(585.5, 39.73) * mm, "mid": v(585.15, 41.47) * mm, "end": v(583.56, 42.25) * mm});
            skLineSegment(sketch, "E124.6.0.16", {"start": v(639, 42.25) * mm, "end": v(616.44, 42.25) * mm});
            skLineSegment(sketch, "E124.6.0.17", {"start": v(624.26, 15.8) * mm, "end": v(643.43, 10.67) * mm});
            skArc(sketch, "E124.6.0.18", {"start": v(639.73, 14.5) * mm, "mid": v(641.47, 14.85) * mm, "end": v(642.25, 16.44) * mm});
            skLineSegment(sketch, "E124.6.0.19", {"start": v(583.56, 42.25) * mm, "end": v(561, 42.25) * mm});
            skArc(sketch, "E124.6.0.20", {"start": v(591.14, -23.09) * mm, "mid": v(600, -25) * mm, "end": v(608.86, -23.09) * mm});
            skLineSegment(sketch, "E124.6.0.21", {"start": v(560.27, 14.5) * mm, "end": v(575.52, 18.6) * mm});
            skArc(sketch, "E124.6.0.22", {"start": v(557.75, 16.44) * mm, "mid": v(558.53, 14.85) * mm, "end": v(560.27, 14.5) * mm});
            skArc(sketch, "E124.6.0.23", {"start": v(608.86, 23.09) * mm, "mid": v(609.06, 23.02) * mm, "end": v(609.27, 23) * mm});
            skArc(sketch, "E124.6.0.24", {"start": v(620.25, 7.4) * mm, "mid": v(620.26, 7.23) * mm, "end": v(620.3, 7.07) * mm});
            skArc(sketch, "E124.6.0.25", {"start": v(614.5, -39.73) * mm, "mid": v(614.85, -41.47) * mm, "end": v(616.44, -42.25) * mm});
            skArc(sketch, "E124.6.0.26", {"start": v(620.53, -23) * mm, "mid": v(619.3, -23.41) * mm, "end": v(618.6, -24.48) * mm});
            skArc(sketch, "E124.6.0.27", {"start": v(579.75, -7.4) * mm, "mid": v(579.74, -7.23) * mm, "end": v(579.7, -7.07) * mm});
            skArc(sketch, "E124.6.0.28", {"start": v(639, -42.25) * mm, "mid": v(641.3, -41.3) * mm, "end": v(642.25, -39) * mm});
            skLineSegment(sketch, "E124.6.0.29", {"start": v(616.44, -42.25) * mm, "end": v(639, -42.25) * mm});
            skArc(sketch, "E124.6.0.30", {"start": v(645, -11.88) * mm, "mid": v(644.51, -10.89) * mm, "end": v(643.43, -10.67) * mm});
            skArc(sketch, "E124.6.0.31", {"start": v(583.56, -42.25) * mm, "mid": v(585.15, -41.47) * mm, "end": v(585.5, -39.73) * mm});
            skArc(sketch, "E124.6.0.32", {"start": v(555, 11.88) * mm, "mid": v(555.49, 10.89) * mm, "end": v(556.57, 10.67) * mm});
            skLineSegment(sketch, "E124.6.0.33", {"start": v(580.75, -20.25) * mm, "end": v(592.6, -20.25) * mm});
            skArc(sketch, "E124.6.0.34", {"start": v(608.86, 23.09) * mm, "mid": v(600, 25) * mm, "end": v(591.14, 23.09) * mm});
            skArc(sketch, "E124.6.0.35", {"start": v(639, -45) * mm, "mid": v(643.24, -43.24) * mm, "end": v(645, -39) * mm});
            skLineSegment(sketch, "E124.6.0.36", {"start": v(639.73, -14.5) * mm, "end": v(624.48, -18.6) * mm});
            skLineSegment(sketch, "E124.6.0.37", {"start": v(624.48, 18.6) * mm, "end": v(639.73, 14.5) * mm});
            skArc(sketch, "E124.6.0.38", {"start": v(620.3, -7.07) * mm, "mid": v(620.26, -7.23) * mm, "end": v(620.25, -7.4) * mm});
            skArc(sketch, "E124.6.0.39", {"start": v(616.44, 42.25) * mm, "mid": v(614.85, 41.47) * mm, "end": v(614.5, 39.73) * mm});
            skArc(sketch, "E124.6.0.40", {"start": v(623.09, -8.86) * mm, "mid": v(625, 0) * mm, "end": v(623.09, 8.86) * mm});
            skArc(sketch, "E124.6.0.41", {"start": v(618.6, 24.48) * mm, "mid": v(619.3, 23.41) * mm, "end": v(620.53, 23) * mm});
            skArc(sketch, "E124.6.0.42", {"start": v(556.57, -10.67) * mm, "mid": v(555.49, -10.89) * mm, "end": v(555, -11.88) * mm});
            skLineSegment(sketch, "E124.6.0.43", {"start": v(577, -21) * mm, "end": v(577, -20.53) * mm});
            skLineSegment(sketch, "E124.6.0.44", {"start": v(561, -42.25) * mm, "end": v(583.56, -42.25) * mm});
            skLineSegment(sketch, "E124.6.0.45", {"start": v(585.16, 23) * mm, "end": v(590.73, 23) * mm});
            skLineSegment(sketch, "E124.6.0.46", {"start": v(592.6, 20.25) * mm, "end": v(580.75, 20.25) * mm});
            skLineSegment(sketch, "E124.6.0.47", {"start": v(645, -39) * mm, "end": v(645, -11.88) * mm});
            skLineSegment(sketch, "E124.6.0.48", {"start": v(589.01, -42.25) * mm, "end": v(610.99, -42.25) * mm});
            skLineSegment(sketch, "E124.6.0.49", {"start": v(589.01, 42.25) * mm, "end": v(584.2, 24.26) * mm});
            skLineSegment(sketch, "E124.6.0.50", {"start": v(577, 14.84) * mm, "end": v(577, 9.27) * mm});
            skArc(sketch, "E124.6.0.51", {"start": v(620.25, 19.25) * mm, "mid": v(619.96, 19.96) * mm, "end": v(619.25, 20.25) * mm});
            skArc(sketch, "E124.6.0.52", {"start": v(592.93, -20.3) * mm, "mid": v(600, -21.5) * mm, "end": v(607.07, -20.3) * mm});
            skArc(sketch, "E124.6.0.53", {"start": v(607.07, 20.3) * mm, "mid": v(600, 21.5) * mm, "end": v(592.93, 20.3) * mm});
            skArc(sketch, "E124.6.0.54", {"start": v(577, -21) * mm, "mid": v(577.59, -22.41) * mm, "end": v(579, -23) * mm});
            skLineSegment(sketch, "E124.6.0.55", {"start": v(581.4, 24.48) * mm, "end": v(585.5, 39.73) * mm});
            skArc(sketch, "E124.6.0.56", {"start": v(607.4, -20.25) * mm, "mid": v(607.23, -20.26) * mm, "end": v(607.07, -20.3) * mm});
            skLineSegment(sketch, "E124.6.0.57", {"start": v(619.25, 20.25) * mm, "end": v(607.4, 20.25) * mm});
            skArc(sketch, "E124.6.0.58", {"start": v(576.91, 8.86) * mm, "mid": v(576.98, 9.06) * mm, "end": v(577, 9.27) * mm});
            skArc(sketch, "E124.6.0.59", {"start": v(619.25, -20.25) * mm, "mid": v(619.96, -19.96) * mm, "end": v(620.25, -19.25) * mm});
            skArc(sketch, "E124.6.0.60", {"start": v(623.09, -8.86) * mm, "mid": v(623.02, -9.06) * mm, "end": v(623, -9.27) * mm});
            skLineSegment(sketch, "E124.6.0.61", {"start": v(614.5, 39.73) * mm, "end": v(618.6, 24.48) * mm});
            skArc(sketch, "E124.6.0.62", {"start": v(580.75, 20.25) * mm, "mid": v(580.04, 19.96) * mm, "end": v(579.75, 19.25) * mm});
            skLineSegment(sketch, "E124.6.0.63", {"start": v(556.57, 10.67) * mm, "end": v(575.74, 15.8) * mm});
            skLineSegment(sketch, "E124.6.0.64", {"start": v(620.25, 7.4) * mm, "end": v(620.25, 19.25) * mm});
            skLineSegment(sketch, "E124.6.0.65", {"start": v(642.25, -39) * mm, "end": v(642.25, -16.44) * mm});
            skArc(sketch, "E124.6.0.66", {"start": v(591.14, -23.09) * mm, "mid": v(590.94, -23.02) * mm, "end": v(590.73, -23) * mm});
            skArc(sketch, "E124.6.0.67", {"start": v(620.3, -7.07) * mm, "mid": v(621.5, 0) * mm, "end": v(620.3, 7.07) * mm});
            skArc(sketch, "E124.6.0.68", {"start": v(560.27, -14.5) * mm, "mid": v(558.53, -14.85) * mm, "end": v(557.75, -16.44) * mm});
            skArc(sketch, "E124.6.0.69", {"start": v(643.43, 10.67) * mm, "mid": v(644.51, 10.89) * mm, "end": v(645, 11.88) * mm});
            skArc(sketch, "E124.6.0.70", {"start": v(590.73, 23) * mm, "mid": v(590.94, 23.02) * mm, "end": v(591.14, 23.09) * mm});
            skLineSegment(sketch, "E124.6.0.71", {"start": v(643.43, -10.67) * mm, "end": v(624.26, -15.8) * mm});
            skLineSegment(sketch, "E124.6.0.72", {"start": v(614.84, -23) * mm, "end": v(609.27, -23) * mm});
            skLineSegment(sketch, "E124.6.0.73", {"start": v(585.5, -39.73) * mm, "end": v(581.4, -24.48) * mm});
            skLineSegment(sketch, "E124.6.0.74", {"start": v(610.99, -42.25) * mm, "end": v(615.8, -24.26) * mm});
            skLineSegment(sketch, "E124.6.0.75", {"start": v(579.75, -7.4) * mm, "end": v(579.75, -19.25) * mm});
            skLineSegment(sketch, "E124.6.0.76", {"start": v(577, -9.27) * mm, "end": v(577, -14.84) * mm});
            skLineSegment(sketch, "E124.6.0.77", {"start": v(621, -23) * mm, "end": v(620.53, -23) * mm});
            skArc(sketch, "E124.6.0.78", {"start": v(615.8, -24.26) * mm, "mid": v(615.64, -23.4) * mm, "end": v(614.84, -23) * mm});
            skArc(sketch, "E124.6.0.79", {"start": v(614.84, 23) * mm, "mid": v(615.64, 23.4) * mm, "end": v(615.8, 24.26) * mm});
            skArc(sketch, "E124.6.0.80", {"start": v(579, 23) * mm, "mid": v(577.59, 22.41) * mm, "end": v(577, 21) * mm});
            skLineSegment(sketch, "E124.6.0.81", {"start": v(618.6, -24.48) * mm, "end": v(614.5, -39.73) * mm});
            skArc(sketch, "E124.6.0.82", {"start": v(576.91, 8.86) * mm, "mid": v(575, 0) * mm, "end": v(576.91, -8.86) * mm});
            skArc(sketch, "E124.6.0.83", {"start": v(623, -14.84) * mm, "mid": v(623.4, -15.64) * mm, "end": v(624.26, -15.8) * mm});
            skArc(sketch, "E124.6.0.84", {"start": v(592.6, 20.25) * mm, "mid": v(592.77, 20.26) * mm, "end": v(592.93, 20.3) * mm});
            skLineSegment(sketch, "E124.6.0.85", {"start": v(579.47, -23) * mm, "end": v(579, -23) * mm});
            skLineSegment(sketch, "E124.6.0.86", {"start": v(615.8, 24.26) * mm, "end": v(610.99, 42.25) * mm});
            skArc(sketch, "E124.6.0.87", {"start": v(623, 20.53) * mm, "mid": v(623.41, 19.3) * mm, "end": v(624.48, 18.6) * mm});
            skArc(sketch, "E124.6.0.88", {"start": v(609.27, -23) * mm, "mid": v(609.06, -23.02) * mm, "end": v(608.86, -23.09) * mm});
            skLineSegment(sketch, "E124.6.0.89", {"start": v(584.2, -24.26) * mm, "end": v(589.01, -42.25) * mm});
            skArc(sketch, "E124.6.0.90", {"start": v(592.93, -20.3) * mm, "mid": v(592.77, -20.26) * mm, "end": v(592.6, -20.25) * mm});
            skArc(sketch, "E124.6.0.91", {"start": v(642.25, -16.44) * mm, "mid": v(641.47, -14.85) * mm, "end": v(639.73, -14.5) * mm});
            skLineSegment(sketch, "E124.6.0.92", {"start": v(575.52, -18.6) * mm, "end": v(560.27, -14.5) * mm});
            skLineSegment(sketch, "E124.6.0.93", {"start": v(623, 9.27) * mm, "end": v(623, 14.84) * mm});
            skArc(sketch, "E124.6.0.94", {"start": v(607.07, 20.3) * mm, "mid": v(607.23, 20.26) * mm, "end": v(607.4, 20.25) * mm});
            skLineSegment(sketch, "E124.6.0.95", {"start": v(609.27, 23) * mm, "end": v(614.84, 23) * mm});
            skArc(sketch, "E124.6.0.96", {"start": v(621, -23) * mm, "mid": v(622.41, -22.41) * mm, "end": v(623, -21) * mm});
            skArc(sketch, "E124.6.0.97", {"start": v(577, -20.53) * mm, "mid": v(576.59, -19.3) * mm, "end": v(575.52, -18.6) * mm});
            skLineSegment(sketch, "E124.6.0.98", {"start": v(579, 23) * mm, "end": v(579.47, 23) * mm});
            skLineSegment(sketch, "E124.6.0.99", {"start": v(620.25, -19.25) * mm, "end": v(620.25, -7.4) * mm});
            skArc(sketch, "E124.6.0.100", {"start": v(584.2, 24.26) * mm, "mid": v(584.36, 23.4) * mm, "end": v(585.16, 23) * mm});
            skLineSegment(sketch, "E124.6.0.101", {"start": v(607.4, -20.25) * mm, "end": v(619.25, -20.25) * mm});
            skLineSegment(sketch, "E124.6.0.102", {"start": v(623, 21) * mm, "end": v(623, 20.53) * mm});
            skLineSegment(sketch, "E124.6.0.103", {"start": v(590.73, -23) * mm, "end": v(585.16, -23) * mm});
            skLineSegment(sketch, "E124.6.0.104", {"start": v(575.74, -15.8) * mm, "end": v(556.57, -10.67) * mm});
            skArc(sketch, "E124.6.0.105", {"start": v(579.7, 7.07) * mm, "mid": v(578.5, 0) * mm, "end": v(579.7, -7.07) * mm});
            skArc(sketch, "E124.6.0.106", {"start": v(623, 9.27) * mm, "mid": v(623.02, 9.06) * mm, "end": v(623.09, 8.86) * mm});
            skArc(sketch, "E124.6.0.107", {"start": v(581.4, -24.48) * mm, "mid": v(580.7, -23.41) * mm, "end": v(579.47, -23) * mm});
            skLineSegment(sketch, "E124.6.0.108", {"start": v(623, -20.53) * mm, "end": v(623, -21) * mm});
            skArc(sketch, "E124.6.0.109", {"start": v(579.47, 23) * mm, "mid": v(580.7, 23.41) * mm, "end": v(581.4, 24.48) * mm});
            skArc(sketch, "E124.6.0.110", {"start": v(577, -9.27) * mm, "mid": v(576.98, -9.06) * mm, "end": v(576.91, -8.86) * mm});
            skLineSegment(sketch, "E124.6.0.111", {"start": v(623, -14.84) * mm, "end": v(623, -9.27) * mm});
            skLineSegment(sketch, "E124.6.0.112", {"start": v(620.53, 23) * mm, "end": v(621, 23) * mm});
            skArc(sketch, "E124.6.0.113", {"start": v(575.52, 18.6) * mm, "mid": v(576.59, 19.3) * mm, "end": v(577, 20.53) * mm});
            skArc(sketch, "E124.6.0.114", {"start": v(585.16, -23) * mm, "mid": v(584.36, -23.4) * mm, "end": v(584.2, -24.26) * mm});
            skArc(sketch, "E124.6.0.115", {"start": v(575.74, -15.8) * mm, "mid": v(576.6, -15.64) * mm, "end": v(577, -14.84) * mm});
            skArc(sketch, "E124.6.0.116", {"start": v(624.48, -18.6) * mm, "mid": v(623.41, -19.3) * mm, "end": v(623, -20.53) * mm});
            skLineSegment(sketch, "E124.6.0.117", {"start": v(579.75, 19.25) * mm, "end": v(579.75, 7.4) * mm});
            skArc(sketch, "E124.6.0.118", {"start": v(579.75, -19.25) * mm, "mid": v(580.04, -19.96) * mm, "end": v(580.75, -20.25) * mm});
            skArc(sketch, "E124.6.0.119", {"start": v(623, 21) * mm, "mid": v(622.41, 22.41) * mm, "end": v(621, 23) * mm});
            skArc(sketch, "E124.6.0.120", {"start": v(624.26, 15.8) * mm, "mid": v(623.4, 15.64) * mm, "end": v(623, 14.84) * mm});
            skArc(sketch, "E124.6.0.121", {"start": v(577, 14.84) * mm, "mid": v(576.6, 15.64) * mm, "end": v(575.74, 15.8) * mm});
            skArc(sketch, "E124.6.0.122", {"start": v(579.7, 7.07) * mm, "mid": v(579.74, 7.23) * mm, "end": v(579.75, 7.4) * mm});
            skLineSegment(sketch, "E124.6.0.123", {"start": v(577, 20.53) * mm, "end": v(577, 21) * mm});
            skArc(sketch, "E124.7.0.0", {"start": v(745, 39) * mm, "mid": v(743.24, 43.24) * mm, "end": v(739, 45) * mm});
            skLineSegment(sketch, "E124.7.0.1", {"start": v(655, -11.88) * mm, "end": v(655, -39) * mm});
            skLineSegment(sketch, "E124.7.0.2", {"start": v(745, 11.88) * mm, "end": v(745, 39) * mm});
            skArc(sketch, "E124.7.0.3", {"start": v(655, -39) * mm, "mid": v(656.76, -43.24) * mm, "end": v(661, -45) * mm});
            skLineSegment(sketch, "E124.7.0.4", {"start": v(657.75, -16.44) * mm, "end": v(657.75, -39) * mm});
            skLineSegment(sketch, "E124.7.0.5", {"start": v(661, -45) * mm, "end": v(739, -45) * mm});
            skArc(sketch, "E124.7.0.6", {"start": v(657.75, -39) * mm, "mid": v(658.7, -41.3) * mm, "end": v(661, -42.25) * mm});
            skLineSegment(sketch, "E124.7.0.7", {"start": v(655, 39) * mm, "end": v(655, 11.88) * mm});
            skArc(sketch, "E124.7.0.8", {"start": v(661, 42.25) * mm, "mid": v(658.7, 41.3) * mm, "end": v(657.75, 39) * mm});
            skArc(sketch, "E124.7.0.9", {"start": v(661, 45) * mm, "mid": v(656.76, 43.24) * mm, "end": v(655, 39) * mm});
            skLineSegment(sketch, "E124.7.0.10", {"start": v(657.75, 39) * mm, "end": v(657.75, 16.44) * mm});
            skArc(sketch, "E124.7.0.11", {"start": v(742.25, 39) * mm, "mid": v(741.3, 41.3) * mm, "end": v(739, 42.25) * mm});
            skLineSegment(sketch, "E124.7.0.12", {"start": v(739, 45) * mm, "end": v(661, 45) * mm});
            skLineSegment(sketch, "E124.7.0.13", {"start": v(742.25, 16.44) * mm, "end": v(742.25, 39) * mm});
            skLineSegment(sketch, "E124.7.0.14", {"start": v(710.99, 42.25) * mm, "end": v(689.01, 42.25) * mm});
            skArc(sketch, "E124.7.0.15", {"start": v(685.5, 39.73) * mm, "mid": v(685.15, 41.47) * mm, "end": v(683.56, 42.25) * mm});
            skLineSegment(sketch, "E124.7.0.16", {"start": v(739, 42.25) * mm, "end": v(716.44, 42.25) * mm});
            skLineSegment(sketch, "E124.7.0.17", {"start": v(724.26, 15.8) * mm, "end": v(743.43, 10.67) * mm});
            skArc(sketch, "E124.7.0.18", {"start": v(739.73, 14.5) * mm, "mid": v(741.47, 14.85) * mm, "end": v(742.25, 16.44) * mm});
            skLineSegment(sketch, "E124.7.0.19", {"start": v(683.56, 42.25) * mm, "end": v(661, 42.25) * mm});
            skArc(sketch, "E124.7.0.20", {"start": v(691.14, -23.09) * mm, "mid": v(700, -25) * mm, "end": v(708.86, -23.09) * mm});
            skLineSegment(sketch, "E124.7.0.21", {"start": v(660.27, 14.5) * mm, "end": v(675.52, 18.6) * mm});
            skArc(sketch, "E124.7.0.22", {"start": v(657.75, 16.44) * mm, "mid": v(658.53, 14.85) * mm, "end": v(660.27, 14.5) * mm});
            skArc(sketch, "E124.7.0.23", {"start": v(708.86, 23.09) * mm, "mid": v(709.06, 23.02) * mm, "end": v(709.27, 23) * mm});
            skArc(sketch, "E124.7.0.24", {"start": v(720.25, 7.4) * mm, "mid": v(720.26, 7.23) * mm, "end": v(720.3, 7.07) * mm});
            skArc(sketch, "E124.7.0.25", {"start": v(714.5, -39.73) * mm, "mid": v(714.85, -41.47) * mm, "end": v(716.44, -42.25) * mm});
            skArc(sketch, "E124.7.0.26", {"start": v(720.53, -23) * mm, "mid": v(719.3, -23.41) * mm, "end": v(718.6, -24.48) * mm});
            skArc(sketch, "E124.7.0.27", {"start": v(679.75, -7.4) * mm, "mid": v(679.74, -7.23) * mm, "end": v(679.7, -7.07) * mm});
            skArc(sketch, "E124.7.0.28", {"start": v(739, -42.25) * mm, "mid": v(741.3, -41.3) * mm, "end": v(742.25, -39) * mm});
            skLineSegment(sketch, "E124.7.0.29", {"start": v(716.44, -42.25) * mm, "end": v(739, -42.25) * mm});
            skArc(sketch, "E124.7.0.30", {"start": v(745, -11.88) * mm, "mid": v(744.51, -10.89) * mm, "end": v(743.43, -10.67) * mm});
            skArc(sketch, "E124.7.0.31", {"start": v(683.56, -42.25) * mm, "mid": v(685.15, -41.47) * mm, "end": v(685.5, -39.73) * mm});
            skArc(sketch, "E124.7.0.32", {"start": v(655, 11.88) * mm, "mid": v(655.49, 10.89) * mm, "end": v(656.57, 10.67) * mm});
            skLineSegment(sketch, "E124.7.0.33", {"start": v(680.75, -20.25) * mm, "end": v(692.6, -20.25) * mm});
            skArc(sketch, "E124.7.0.34", {"start": v(708.86, 23.09) * mm, "mid": v(700, 25) * mm, "end": v(691.14, 23.09) * mm});
            skArc(sketch, "E124.7.0.35", {"start": v(739, -45) * mm, "mid": v(743.24, -43.24) * mm, "end": v(745, -39) * mm});
            skLineSegment(sketch, "E124.7.0.36", {"start": v(739.73, -14.5) * mm, "end": v(724.48, -18.6) * mm});
            skLineSegment(sketch, "E124.7.0.37", {"start": v(724.48, 18.6) * mm, "end": v(739.73, 14.5) * mm});
            skArc(sketch, "E124.7.0.38", {"start": v(720.3, -7.07) * mm, "mid": v(720.26, -7.23) * mm, "end": v(720.25, -7.4) * mm});
            skArc(sketch, "E124.7.0.39", {"start": v(716.44, 42.25) * mm, "mid": v(714.85, 41.47) * mm, "end": v(714.5, 39.73) * mm});
            skArc(sketch, "E124.7.0.40", {"start": v(723.09, -8.86) * mm, "mid": v(725, 0) * mm, "end": v(723.09, 8.86) * mm});
            skArc(sketch, "E124.7.0.41", {"start": v(718.6, 24.48) * mm, "mid": v(719.3, 23.41) * mm, "end": v(720.53, 23) * mm});
            skArc(sketch, "E124.7.0.42", {"start": v(656.57, -10.67) * mm, "mid": v(655.49, -10.89) * mm, "end": v(655, -11.88) * mm});
            skLineSegment(sketch, "E124.7.0.43", {"start": v(677, -21) * mm, "end": v(677, -20.53) * mm});
            skLineSegment(sketch, "E124.7.0.44", {"start": v(661, -42.25) * mm, "end": v(683.56, -42.25) * mm});
            skLineSegment(sketch, "E124.7.0.45", {"start": v(685.16, 23) * mm, "end": v(690.73, 23) * mm});
            skLineSegment(sketch, "E124.7.0.46", {"start": v(692.6, 20.25) * mm, "end": v(680.75, 20.25) * mm});
            skLineSegment(sketch, "E124.7.0.47", {"start": v(745, -39) * mm, "end": v(745, -11.88) * mm});
            skLineSegment(sketch, "E124.7.0.48", {"start": v(689.01, -42.25) * mm, "end": v(710.99, -42.25) * mm});
            skLineSegment(sketch, "E124.7.0.49", {"start": v(689.01, 42.25) * mm, "end": v(684.2, 24.26) * mm});
            skLineSegment(sketch, "E124.7.0.50", {"start": v(677, 14.84) * mm, "end": v(677, 9.27) * mm});
            skArc(sketch, "E124.7.0.51", {"start": v(720.25, 19.25) * mm, "mid": v(719.96, 19.96) * mm, "end": v(719.25, 20.25) * mm});
            skArc(sketch, "E124.7.0.52", {"start": v(692.93, -20.3) * mm, "mid": v(700, -21.5) * mm, "end": v(707.07, -20.3) * mm});
            skArc(sketch, "E124.7.0.53", {"start": v(707.07, 20.3) * mm, "mid": v(700, 21.5) * mm, "end": v(692.93, 20.3) * mm});
            skArc(sketch, "E124.7.0.54", {"start": v(677, -21) * mm, "mid": v(677.59, -22.41) * mm, "end": v(679, -23) * mm});
            skLineSegment(sketch, "E124.7.0.55", {"start": v(681.4, 24.48) * mm, "end": v(685.5, 39.73) * mm});
            skArc(sketch, "E124.7.0.56", {"start": v(707.4, -20.25) * mm, "mid": v(707.23, -20.26) * mm, "end": v(707.07, -20.3) * mm});
            skLineSegment(sketch, "E124.7.0.57", {"start": v(719.25, 20.25) * mm, "end": v(707.4, 20.25) * mm});
            skArc(sketch, "E124.7.0.58", {"start": v(676.91, 8.86) * mm, "mid": v(676.98, 9.06) * mm, "end": v(677, 9.27) * mm});
            skArc(sketch, "E124.7.0.59", {"start": v(719.25, -20.25) * mm, "mid": v(719.96, -19.96) * mm, "end": v(720.25, -19.25) * mm});
            skArc(sketch, "E124.7.0.60", {"start": v(723.09, -8.86) * mm, "mid": v(723.02, -9.06) * mm, "end": v(723, -9.27) * mm});
            skLineSegment(sketch, "E124.7.0.61", {"start": v(714.5, 39.73) * mm, "end": v(718.6, 24.48) * mm});
            skArc(sketch, "E124.7.0.62", {"start": v(680.75, 20.25) * mm, "mid": v(680.04, 19.96) * mm, "end": v(679.75, 19.25) * mm});
            skLineSegment(sketch, "E124.7.0.63", {"start": v(656.57, 10.67) * mm, "end": v(675.74, 15.8) * mm});
            skLineSegment(sketch, "E124.7.0.64", {"start": v(720.25, 7.4) * mm, "end": v(720.25, 19.25) * mm});
            skLineSegment(sketch, "E124.7.0.65", {"start": v(742.25, -39) * mm, "end": v(742.25, -16.44) * mm});
            skArc(sketch, "E124.7.0.66", {"start": v(691.14, -23.09) * mm, "mid": v(690.94, -23.02) * mm, "end": v(690.73, -23) * mm});
            skArc(sketch, "E124.7.0.67", {"start": v(720.3, -7.07) * mm, "mid": v(721.5, 0) * mm, "end": v(720.3, 7.07) * mm});
            skArc(sketch, "E124.7.0.68", {"start": v(660.27, -14.5) * mm, "mid": v(658.53, -14.85) * mm, "end": v(657.75, -16.44) * mm});
            skArc(sketch, "E124.7.0.69", {"start": v(743.43, 10.67) * mm, "mid": v(744.51, 10.89) * mm, "end": v(745, 11.88) * mm});
            skArc(sketch, "E124.7.0.70", {"start": v(690.73, 23) * mm, "mid": v(690.94, 23.02) * mm, "end": v(691.14, 23.09) * mm});
            skLineSegment(sketch, "E124.7.0.71", {"start": v(743.43, -10.67) * mm, "end": v(724.26, -15.8) * mm});
            skLineSegment(sketch, "E124.7.0.72", {"start": v(714.84, -23) * mm, "end": v(709.27, -23) * mm});
            skLineSegment(sketch, "E124.7.0.73", {"start": v(685.5, -39.73) * mm, "end": v(681.4, -24.48) * mm});
            skLineSegment(sketch, "E124.7.0.74", {"start": v(710.99, -42.25) * mm, "end": v(715.8, -24.26) * mm});
            skLineSegment(sketch, "E124.7.0.75", {"start": v(679.75, -7.4) * mm, "end": v(679.75, -19.25) * mm});
            skLineSegment(sketch, "E124.7.0.76", {"start": v(677, -9.27) * mm, "end": v(677, -14.84) * mm});
            skLineSegment(sketch, "E124.7.0.77", {"start": v(721, -23) * mm, "end": v(720.53, -23) * mm});
            skArc(sketch, "E124.7.0.78", {"start": v(715.8, -24.26) * mm, "mid": v(715.64, -23.4) * mm, "end": v(714.84, -23) * mm});
            skArc(sketch, "E124.7.0.79", {"start": v(714.84, 23) * mm, "mid": v(715.64, 23.4) * mm, "end": v(715.8, 24.26) * mm});
            skArc(sketch, "E124.7.0.80", {"start": v(679, 23) * mm, "mid": v(677.59, 22.41) * mm, "end": v(677, 21) * mm});
            skLineSegment(sketch, "E124.7.0.81", {"start": v(718.6, -24.48) * mm, "end": v(714.5, -39.73) * mm});
            skArc(sketch, "E124.7.0.82", {"start": v(676.91, 8.86) * mm, "mid": v(675, 0) * mm, "end": v(676.91, -8.86) * mm});
            skArc(sketch, "E124.7.0.83", {"start": v(723, -14.84) * mm, "mid": v(723.4, -15.64) * mm, "end": v(724.26, -15.8) * mm});
            skArc(sketch, "E124.7.0.84", {"start": v(692.6, 20.25) * mm, "mid": v(692.77, 20.26) * mm, "end": v(692.93, 20.3) * mm});
            skLineSegment(sketch, "E124.7.0.85", {"start": v(679.47, -23) * mm, "end": v(679, -23) * mm});
            skLineSegment(sketch, "E124.7.0.86", {"start": v(715.8, 24.26) * mm, "end": v(710.99, 42.25) * mm});
            skArc(sketch, "E124.7.0.87", {"start": v(723, 20.53) * mm, "mid": v(723.41, 19.3) * mm, "end": v(724.48, 18.6) * mm});
            skArc(sketch, "E124.7.0.88", {"start": v(709.27, -23) * mm, "mid": v(709.06, -23.02) * mm, "end": v(708.86, -23.09) * mm});
            skLineSegment(sketch, "E124.7.0.89", {"start": v(684.2, -24.26) * mm, "end": v(689.01, -42.25) * mm});
            skArc(sketch, "E124.7.0.90", {"start": v(692.93, -20.3) * mm, "mid": v(692.77, -20.26) * mm, "end": v(692.6, -20.25) * mm});
            skArc(sketch, "E124.7.0.91", {"start": v(742.25, -16.44) * mm, "mid": v(741.47, -14.85) * mm, "end": v(739.73, -14.5) * mm});
            skLineSegment(sketch, "E124.7.0.92", {"start": v(675.52, -18.6) * mm, "end": v(660.27, -14.5) * mm});
            skLineSegment(sketch, "E124.7.0.93", {"start": v(723, 9.27) * mm, "end": v(723, 14.84) * mm});
            skArc(sketch, "E124.7.0.94", {"start": v(707.07, 20.3) * mm, "mid": v(707.23, 20.26) * mm, "end": v(707.4, 20.25) * mm});
            skLineSegment(sketch, "E124.7.0.95", {"start": v(709.27, 23) * mm, "end": v(714.84, 23) * mm});
            skArc(sketch, "E124.7.0.96", {"start": v(721, -23) * mm, "mid": v(722.41, -22.41) * mm, "end": v(723, -21) * mm});
            skArc(sketch, "E124.7.0.97", {"start": v(677, -20.53) * mm, "mid": v(676.59, -19.3) * mm, "end": v(675.52, -18.6) * mm});
            skLineSegment(sketch, "E124.7.0.98", {"start": v(679, 23) * mm, "end": v(679.47, 23) * mm});
            skLineSegment(sketch, "E124.7.0.99", {"start": v(720.25, -19.25) * mm, "end": v(720.25, -7.4) * mm});
            skArc(sketch, "E124.7.0.100", {"start": v(684.2, 24.26) * mm, "mid": v(684.36, 23.4) * mm, "end": v(685.16, 23) * mm});
            skLineSegment(sketch, "E124.7.0.101", {"start": v(707.4, -20.25) * mm, "end": v(719.25, -20.25) * mm});
            skLineSegment(sketch, "E124.7.0.102", {"start": v(723, 21) * mm, "end": v(723, 20.53) * mm});
            skLineSegment(sketch, "E124.7.0.103", {"start": v(690.73, -23) * mm, "end": v(685.16, -23) * mm});
            skLineSegment(sketch, "E124.7.0.104", {"start": v(675.74, -15.8) * mm, "end": v(656.57, -10.67) * mm});
            skArc(sketch, "E124.7.0.105", {"start": v(679.7, 7.07) * mm, "mid": v(678.5, 0) * mm, "end": v(679.7, -7.07) * mm});
            skArc(sketch, "E124.7.0.106", {"start": v(723, 9.27) * mm, "mid": v(723.02, 9.06) * mm, "end": v(723.09, 8.86) * mm});
            skArc(sketch, "E124.7.0.107", {"start": v(681.4, -24.48) * mm, "mid": v(680.7, -23.41) * mm, "end": v(679.47, -23) * mm});
            skLineSegment(sketch, "E124.7.0.108", {"start": v(723, -20.53) * mm, "end": v(723, -21) * mm});
            skArc(sketch, "E124.7.0.109", {"start": v(679.47, 23) * mm, "mid": v(680.7, 23.41) * mm, "end": v(681.4, 24.48) * mm});
            skArc(sketch, "E124.7.0.110", {"start": v(677, -9.27) * mm, "mid": v(676.98, -9.06) * mm, "end": v(676.91, -8.86) * mm});
            skLineSegment(sketch, "E124.7.0.111", {"start": v(723, -14.84) * mm, "end": v(723, -9.27) * mm});
            skLineSegment(sketch, "E124.7.0.112", {"start": v(720.53, 23) * mm, "end": v(721, 23) * mm});
            skArc(sketch, "E124.7.0.113", {"start": v(675.52, 18.6) * mm, "mid": v(676.59, 19.3) * mm, "end": v(677, 20.53) * mm});
            skArc(sketch, "E124.7.0.114", {"start": v(685.16, -23) * mm, "mid": v(684.36, -23.4) * mm, "end": v(684.2, -24.26) * mm});
            skArc(sketch, "E124.7.0.115", {"start": v(675.74, -15.8) * mm, "mid": v(676.6, -15.64) * mm, "end": v(677, -14.84) * mm});
            skArc(sketch, "E124.7.0.116", {"start": v(724.48, -18.6) * mm, "mid": v(723.41, -19.3) * mm, "end": v(723, -20.53) * mm});
            skLineSegment(sketch, "E124.7.0.117", {"start": v(679.75, 19.25) * mm, "end": v(679.75, 7.4) * mm});
            skArc(sketch, "E124.7.0.118", {"start": v(679.75, -19.25) * mm, "mid": v(680.04, -19.96) * mm, "end": v(680.75, -20.25) * mm});
            skArc(sketch, "E124.7.0.119", {"start": v(723, 21) * mm, "mid": v(722.41, 22.41) * mm, "end": v(721, 23) * mm});
            skArc(sketch, "E124.7.0.120", {"start": v(724.26, 15.8) * mm, "mid": v(723.4, 15.64) * mm, "end": v(723, 14.84) * mm});
            skArc(sketch, "E124.7.0.121", {"start": v(677, 14.84) * mm, "mid": v(676.6, 15.64) * mm, "end": v(675.74, 15.8) * mm});
            skArc(sketch, "E124.7.0.122", {"start": v(679.7, 7.07) * mm, "mid": v(679.74, 7.23) * mm, "end": v(679.75, 7.4) * mm});
            skLineSegment(sketch, "E124.7.0.123", {"start": v(677, 20.53) * mm, "end": v(677, 21) * mm});
            skArc(sketch, "E124.8.0.0", {"start": v(845, 39) * mm, "mid": v(843.24, 43.24) * mm, "end": v(839, 45) * mm});
            skLineSegment(sketch, "E124.8.0.1", {"start": v(755, -11.88) * mm, "end": v(755, -39) * mm});
            skLineSegment(sketch, "E124.8.0.2", {"start": v(845, 11.88) * mm, "end": v(845, 39) * mm});
            skArc(sketch, "E124.8.0.3", {"start": v(755, -39) * mm, "mid": v(756.76, -43.24) * mm, "end": v(761, -45) * mm});
            skLineSegment(sketch, "E124.8.0.4", {"start": v(757.75, -16.44) * mm, "end": v(757.75, -39) * mm});
            skLineSegment(sketch, "E124.8.0.5", {"start": v(761, -45) * mm, "end": v(839, -45) * mm});
            skArc(sketch, "E124.8.0.6", {"start": v(757.75, -39) * mm, "mid": v(758.7, -41.3) * mm, "end": v(761, -42.25) * mm});
            skLineSegment(sketch, "E124.8.0.7", {"start": v(755, 39) * mm, "end": v(755, 11.88) * mm});
            skArc(sketch, "E124.8.0.8", {"start": v(761, 42.25) * mm, "mid": v(758.7, 41.3) * mm, "end": v(757.75, 39) * mm});
            skArc(sketch, "E124.8.0.9", {"start": v(761, 45) * mm, "mid": v(756.76, 43.24) * mm, "end": v(755, 39) * mm});
            skLineSegment(sketch, "E124.8.0.10", {"start": v(757.75, 39) * mm, "end": v(757.75, 16.44) * mm});
            skArc(sketch, "E124.8.0.11", {"start": v(842.25, 39) * mm, "mid": v(841.3, 41.3) * mm, "end": v(839, 42.25) * mm});
            skLineSegment(sketch, "E124.8.0.12", {"start": v(839, 45) * mm, "end": v(761, 45) * mm});
            skLineSegment(sketch, "E124.8.0.13", {"start": v(842.25, 16.44) * mm, "end": v(842.25, 39) * mm});
            skLineSegment(sketch, "E124.8.0.14", {"start": v(810.99, 42.25) * mm, "end": v(789.01, 42.25) * mm});
            skArc(sketch, "E124.8.0.15", {"start": v(785.5, 39.73) * mm, "mid": v(785.15, 41.47) * mm, "end": v(783.56, 42.25) * mm});
            skLineSegment(sketch, "E124.8.0.16", {"start": v(839, 42.25) * mm, "end": v(816.44, 42.25) * mm});
            skLineSegment(sketch, "E124.8.0.17", {"start": v(824.26, 15.8) * mm, "end": v(843.43, 10.67) * mm});
            skArc(sketch, "E124.8.0.18", {"start": v(839.73, 14.5) * mm, "mid": v(841.47, 14.85) * mm, "end": v(842.25, 16.44) * mm});
            skLineSegment(sketch, "E124.8.0.19", {"start": v(783.56, 42.25) * mm, "end": v(761, 42.25) * mm});
            skArc(sketch, "E124.8.0.20", {"start": v(791.14, -23.09) * mm, "mid": v(800, -25) * mm, "end": v(808.86, -23.09) * mm});
            skLineSegment(sketch, "E124.8.0.21", {"start": v(760.27, 14.5) * mm, "end": v(775.52, 18.6) * mm});
            skArc(sketch, "E124.8.0.22", {"start": v(757.75, 16.44) * mm, "mid": v(758.53, 14.85) * mm, "end": v(760.27, 14.5) * mm});
            skArc(sketch, "E124.8.0.23", {"start": v(808.86, 23.09) * mm, "mid": v(809.06, 23.02) * mm, "end": v(809.27, 23) * mm});
            skArc(sketch, "E124.8.0.24", {"start": v(820.25, 7.4) * mm, "mid": v(820.26, 7.23) * mm, "end": v(820.3, 7.07) * mm});
            skArc(sketch, "E124.8.0.25", {"start": v(814.5, -39.73) * mm, "mid": v(814.85, -41.47) * mm, "end": v(816.44, -42.25) * mm});
            skArc(sketch, "E124.8.0.26", {"start": v(820.53, -23) * mm, "mid": v(819.3, -23.41) * mm, "end": v(818.6, -24.48) * mm});
            skArc(sketch, "E124.8.0.27", {"start": v(779.75, -7.4) * mm, "mid": v(779.74, -7.23) * mm, "end": v(779.7, -7.07) * mm});
            skArc(sketch, "E124.8.0.28", {"start": v(839, -42.25) * mm, "mid": v(841.3, -41.3) * mm, "end": v(842.25, -39) * mm});
            skLineSegment(sketch, "E124.8.0.29", {"start": v(816.44, -42.25) * mm, "end": v(839, -42.25) * mm});
            skArc(sketch, "E124.8.0.30", {"start": v(845, -11.88) * mm, "mid": v(844.51, -10.89) * mm, "end": v(843.43, -10.67) * mm});
            skArc(sketch, "E124.8.0.31", {"start": v(783.56, -42.25) * mm, "mid": v(785.15, -41.47) * mm, "end": v(785.5, -39.73) * mm});
            skArc(sketch, "E124.8.0.32", {"start": v(755, 11.88) * mm, "mid": v(755.49, 10.89) * mm, "end": v(756.57, 10.67) * mm});
            skLineSegment(sketch, "E124.8.0.33", {"start": v(780.75, -20.25) * mm, "end": v(792.6, -20.25) * mm});
            skArc(sketch, "E124.8.0.34", {"start": v(808.86, 23.09) * mm, "mid": v(800, 25) * mm, "end": v(791.14, 23.09) * mm});
            skArc(sketch, "E124.8.0.35", {"start": v(839, -45) * mm, "mid": v(843.24, -43.24) * mm, "end": v(845, -39) * mm});
            skLineSegment(sketch, "E124.8.0.36", {"start": v(839.73, -14.5) * mm, "end": v(824.48, -18.6) * mm});
            skLineSegment(sketch, "E124.8.0.37", {"start": v(824.48, 18.6) * mm, "end": v(839.73, 14.5) * mm});
            skArc(sketch, "E124.8.0.38", {"start": v(820.3, -7.07) * mm, "mid": v(820.26, -7.23) * mm, "end": v(820.25, -7.4) * mm});
            skArc(sketch, "E124.8.0.39", {"start": v(816.44, 42.25) * mm, "mid": v(814.85, 41.47) * mm, "end": v(814.5, 39.73) * mm});
            skArc(sketch, "E124.8.0.40", {"start": v(823.09, -8.86) * mm, "mid": v(825, 0) * mm, "end": v(823.09, 8.86) * mm});
            skArc(sketch, "E124.8.0.41", {"start": v(818.6, 24.48) * mm, "mid": v(819.3, 23.41) * mm, "end": v(820.53, 23) * mm});
            skArc(sketch, "E124.8.0.42", {"start": v(756.57, -10.67) * mm, "mid": v(755.49, -10.89) * mm, "end": v(755, -11.88) * mm});
            skLineSegment(sketch, "E124.8.0.43", {"start": v(777, -21) * mm, "end": v(777, -20.53) * mm});
            skLineSegment(sketch, "E124.8.0.44", {"start": v(761, -42.25) * mm, "end": v(783.56, -42.25) * mm});
            skLineSegment(sketch, "E124.8.0.45", {"start": v(785.16, 23) * mm, "end": v(790.73, 23) * mm});
            skLineSegment(sketch, "E124.8.0.46", {"start": v(792.6, 20.25) * mm, "end": v(780.75, 20.25) * mm});
            skLineSegment(sketch, "E124.8.0.47", {"start": v(845, -39) * mm, "end": v(845, -11.88) * mm});
            skLineSegment(sketch, "E124.8.0.48", {"start": v(789.01, -42.25) * mm, "end": v(810.99, -42.25) * mm});
            skLineSegment(sketch, "E124.8.0.49", {"start": v(789.01, 42.25) * mm, "end": v(784.2, 24.26) * mm});
            skLineSegment(sketch, "E124.8.0.50", {"start": v(777, 14.84) * mm, "end": v(777, 9.27) * mm});
            skArc(sketch, "E124.8.0.51", {"start": v(820.25, 19.25) * mm, "mid": v(819.96, 19.96) * mm, "end": v(819.25, 20.25) * mm});
            skArc(sketch, "E124.8.0.52", {"start": v(792.93, -20.3) * mm, "mid": v(800, -21.5) * mm, "end": v(807.07, -20.3) * mm});
            skArc(sketch, "E124.8.0.53", {"start": v(807.07, 20.3) * mm, "mid": v(800, 21.5) * mm, "end": v(792.93, 20.3) * mm});
            skArc(sketch, "E124.8.0.54", {"start": v(777, -21) * mm, "mid": v(777.59, -22.41) * mm, "end": v(779, -23) * mm});
            skLineSegment(sketch, "E124.8.0.55", {"start": v(781.4, 24.48) * mm, "end": v(785.5, 39.73) * mm});
            skArc(sketch, "E124.8.0.56", {"start": v(807.4, -20.25) * mm, "mid": v(807.23, -20.26) * mm, "end": v(807.07, -20.3) * mm});
            skLineSegment(sketch, "E124.8.0.57", {"start": v(819.25, 20.25) * mm, "end": v(807.4, 20.25) * mm});
            skArc(sketch, "E124.8.0.58", {"start": v(776.91, 8.86) * mm, "mid": v(776.98, 9.06) * mm, "end": v(777, 9.27) * mm});
            skArc(sketch, "E124.8.0.59", {"start": v(819.25, -20.25) * mm, "mid": v(819.96, -19.96) * mm, "end": v(820.25, -19.25) * mm});
            skArc(sketch, "E124.8.0.60", {"start": v(823.09, -8.86) * mm, "mid": v(823.02, -9.06) * mm, "end": v(823, -9.27) * mm});
            skLineSegment(sketch, "E124.8.0.61", {"start": v(814.5, 39.73) * mm, "end": v(818.6, 24.48) * mm});
            skArc(sketch, "E124.8.0.62", {"start": v(780.75, 20.25) * mm, "mid": v(780.04, 19.96) * mm, "end": v(779.75, 19.25) * mm});
            skLineSegment(sketch, "E124.8.0.63", {"start": v(756.57, 10.67) * mm, "end": v(775.74, 15.8) * mm});
            skLineSegment(sketch, "E124.8.0.64", {"start": v(820.25, 7.4) * mm, "end": v(820.25, 19.25) * mm});
            skLineSegment(sketch, "E124.8.0.65", {"start": v(842.25, -39) * mm, "end": v(842.25, -16.44) * mm});
            skArc(sketch, "E124.8.0.66", {"start": v(791.14, -23.09) * mm, "mid": v(790.94, -23.02) * mm, "end": v(790.73, -23) * mm});
            skArc(sketch, "E124.8.0.67", {"start": v(820.3, -7.07) * mm, "mid": v(821.5, 0) * mm, "end": v(820.3, 7.07) * mm});
            skArc(sketch, "E124.8.0.68", {"start": v(760.27, -14.5) * mm, "mid": v(758.53, -14.85) * mm, "end": v(757.75, -16.44) * mm});
            skArc(sketch, "E124.8.0.69", {"start": v(843.43, 10.67) * mm, "mid": v(844.51, 10.89) * mm, "end": v(845, 11.88) * mm});
            skArc(sketch, "E124.8.0.70", {"start": v(790.73, 23) * mm, "mid": v(790.94, 23.02) * mm, "end": v(791.14, 23.09) * mm});
            skLineSegment(sketch, "E124.8.0.71", {"start": v(843.43, -10.67) * mm, "end": v(824.26, -15.8) * mm});
            skLineSegment(sketch, "E124.8.0.72", {"start": v(814.84, -23) * mm, "end": v(809.27, -23) * mm});
            skLineSegment(sketch, "E124.8.0.73", {"start": v(785.5, -39.73) * mm, "end": v(781.4, -24.48) * mm});
            skLineSegment(sketch, "E124.8.0.74", {"start": v(810.99, -42.25) * mm, "end": v(815.8, -24.26) * mm});
            skLineSegment(sketch, "E124.8.0.75", {"start": v(779.75, -7.4) * mm, "end": v(779.75, -19.25) * mm});
            skLineSegment(sketch, "E124.8.0.76", {"start": v(777, -9.27) * mm, "end": v(777, -14.84) * mm});
            skLineSegment(sketch, "E124.8.0.77", {"start": v(821, -23) * mm, "end": v(820.53, -23) * mm});
            skArc(sketch, "E124.8.0.78", {"start": v(815.8, -24.26) * mm, "mid": v(815.64, -23.4) * mm, "end": v(814.84, -23) * mm});
            skArc(sketch, "E124.8.0.79", {"start": v(814.84, 23) * mm, "mid": v(815.64, 23.4) * mm, "end": v(815.8, 24.26) * mm});
            skArc(sketch, "E124.8.0.80", {"start": v(779, 23) * mm, "mid": v(777.59, 22.41) * mm, "end": v(777, 21) * mm});
            skLineSegment(sketch, "E124.8.0.81", {"start": v(818.6, -24.48) * mm, "end": v(814.5, -39.73) * mm});
            skArc(sketch, "E124.8.0.82", {"start": v(776.91, 8.86) * mm, "mid": v(775, 0) * mm, "end": v(776.91, -8.86) * mm});
            skArc(sketch, "E124.8.0.83", {"start": v(823, -14.84) * mm, "mid": v(823.4, -15.64) * mm, "end": v(824.26, -15.8) * mm});
            skArc(sketch, "E124.8.0.84", {"start": v(792.6, 20.25) * mm, "mid": v(792.77, 20.26) * mm, "end": v(792.93, 20.3) * mm});
            skLineSegment(sketch, "E124.8.0.85", {"start": v(779.47, -23) * mm, "end": v(779, -23) * mm});
            skLineSegment(sketch, "E124.8.0.86", {"start": v(815.8, 24.26) * mm, "end": v(810.99, 42.25) * mm});
            skArc(sketch, "E124.8.0.87", {"start": v(823, 20.53) * mm, "mid": v(823.41, 19.3) * mm, "end": v(824.48, 18.6) * mm});
            skArc(sketch, "E124.8.0.88", {"start": v(809.27, -23) * mm, "mid": v(809.06, -23.02) * mm, "end": v(808.86, -23.09) * mm});
            skLineSegment(sketch, "E124.8.0.89", {"start": v(784.2, -24.26) * mm, "end": v(789.01, -42.25) * mm});
            skArc(sketch, "E124.8.0.90", {"start": v(792.93, -20.3) * mm, "mid": v(792.77, -20.26) * mm, "end": v(792.6, -20.25) * mm});
            skArc(sketch, "E124.8.0.91", {"start": v(842.25, -16.44) * mm, "mid": v(841.47, -14.85) * mm, "end": v(839.73, -14.5) * mm});
            skLineSegment(sketch, "E124.8.0.92", {"start": v(775.52, -18.6) * mm, "end": v(760.27, -14.5) * mm});
            skLineSegment(sketch, "E124.8.0.93", {"start": v(823, 9.27) * mm, "end": v(823, 14.84) * mm});
            skArc(sketch, "E124.8.0.94", {"start": v(807.07, 20.3) * mm, "mid": v(807.23, 20.26) * mm, "end": v(807.4, 20.25) * mm});
            skLineSegment(sketch, "E124.8.0.95", {"start": v(809.27, 23) * mm, "end": v(814.84, 23) * mm});
            skArc(sketch, "E124.8.0.96", {"start": v(821, -23) * mm, "mid": v(822.41, -22.41) * mm, "end": v(823, -21) * mm});
            skArc(sketch, "E124.8.0.97", {"start": v(777, -20.53) * mm, "mid": v(776.59, -19.3) * mm, "end": v(775.52, -18.6) * mm});
            skLineSegment(sketch, "E124.8.0.98", {"start": v(779, 23) * mm, "end": v(779.47, 23) * mm});
            skLineSegment(sketch, "E124.8.0.99", {"start": v(820.25, -19.25) * mm, "end": v(820.25, -7.4) * mm});
            skArc(sketch, "E124.8.0.100", {"start": v(784.2, 24.26) * mm, "mid": v(784.36, 23.4) * mm, "end": v(785.16, 23) * mm});
            skLineSegment(sketch, "E124.8.0.101", {"start": v(807.4, -20.25) * mm, "end": v(819.25, -20.25) * mm});
            skLineSegment(sketch, "E124.8.0.102", {"start": v(823, 21) * mm, "end": v(823, 20.53) * mm});
            skLineSegment(sketch, "E124.8.0.103", {"start": v(790.73, -23) * mm, "end": v(785.16, -23) * mm});
            skLineSegment(sketch, "E124.8.0.104", {"start": v(775.74, -15.8) * mm, "end": v(756.57, -10.67) * mm});
            skArc(sketch, "E124.8.0.105", {"start": v(779.7, 7.07) * mm, "mid": v(778.5, 0) * mm, "end": v(779.7, -7.07) * mm});
            skArc(sketch, "E124.8.0.106", {"start": v(823, 9.27) * mm, "mid": v(823.02, 9.06) * mm, "end": v(823.09, 8.86) * mm});
            skArc(sketch, "E124.8.0.107", {"start": v(781.4, -24.48) * mm, "mid": v(780.7, -23.41) * mm, "end": v(779.47, -23) * mm});
            skLineSegment(sketch, "E124.8.0.108", {"start": v(823, -20.53) * mm, "end": v(823, -21) * mm});
            skArc(sketch, "E124.8.0.109", {"start": v(779.47, 23) * mm, "mid": v(780.7, 23.41) * mm, "end": v(781.4, 24.48) * mm});
            skArc(sketch, "E124.8.0.110", {"start": v(777, -9.27) * mm, "mid": v(776.98, -9.06) * mm, "end": v(776.91, -8.86) * mm});
            skLineSegment(sketch, "E124.8.0.111", {"start": v(823, -14.84) * mm, "end": v(823, -9.27) * mm});
            skLineSegment(sketch, "E124.8.0.112", {"start": v(820.53, 23) * mm, "end": v(821, 23) * mm});
            skArc(sketch, "E124.8.0.113", {"start": v(775.52, 18.6) * mm, "mid": v(776.59, 19.3) * mm, "end": v(777, 20.53) * mm});
            skArc(sketch, "E124.8.0.114", {"start": v(785.16, -23) * mm, "mid": v(784.36, -23.4) * mm, "end": v(784.2, -24.26) * mm});
            skArc(sketch, "E124.8.0.115", {"start": v(775.74, -15.8) * mm, "mid": v(776.6, -15.64) * mm, "end": v(777, -14.84) * mm});
            skArc(sketch, "E124.8.0.116", {"start": v(824.48, -18.6) * mm, "mid": v(823.41, -19.3) * mm, "end": v(823, -20.53) * mm});
            skLineSegment(sketch, "E124.8.0.117", {"start": v(779.75, 19.25) * mm, "end": v(779.75, 7.4) * mm});
            skArc(sketch, "E124.8.0.118", {"start": v(779.75, -19.25) * mm, "mid": v(780.04, -19.96) * mm, "end": v(780.75, -20.25) * mm});
            skArc(sketch, "E124.8.0.119", {"start": v(823, 21) * mm, "mid": v(822.41, 22.41) * mm, "end": v(821, 23) * mm});
            skArc(sketch, "E124.8.0.120", {"start": v(824.26, 15.8) * mm, "mid": v(823.4, 15.64) * mm, "end": v(823, 14.84) * mm});
            skArc(sketch, "E124.8.0.121", {"start": v(777, 14.84) * mm, "mid": v(776.6, 15.64) * mm, "end": v(775.74, 15.8) * mm});
            skArc(sketch, "E124.8.0.122", {"start": v(779.7, 7.07) * mm, "mid": v(779.74, 7.23) * mm, "end": v(779.75, 7.4) * mm});
            skLineSegment(sketch, "E124.8.0.123", {"start": v(777, 20.53) * mm, "end": v(777, 21) * mm});
            skArc(sketch, "E124.9.0.0", {"start": v(945, 39) * mm, "mid": v(943.24, 43.24) * mm, "end": v(939, 45) * mm});
            skLineSegment(sketch, "E124.9.0.1", {"start": v(855, -11.88) * mm, "end": v(855, -39) * mm});
            skLineSegment(sketch, "E124.9.0.2", {"start": v(945, 11.88) * mm, "end": v(945, 39) * mm});
            skArc(sketch, "E124.9.0.3", {"start": v(855, -39) * mm, "mid": v(856.76, -43.24) * mm, "end": v(861, -45) * mm});
            skLineSegment(sketch, "E124.9.0.4", {"start": v(857.75, -16.44) * mm, "end": v(857.75, -39) * mm});
            skLineSegment(sketch, "E124.9.0.5", {"start": v(861, -45) * mm, "end": v(939, -45) * mm});
            skArc(sketch, "E124.9.0.6", {"start": v(857.75, -39) * mm, "mid": v(858.7, -41.3) * mm, "end": v(861, -42.25) * mm});
            skLineSegment(sketch, "E124.9.0.7", {"start": v(855, 39) * mm, "end": v(855, 11.88) * mm});
            skArc(sketch, "E124.9.0.8", {"start": v(861, 42.25) * mm, "mid": v(858.7, 41.3) * mm, "end": v(857.75, 39) * mm});
            skArc(sketch, "E124.9.0.9", {"start": v(861, 45) * mm, "mid": v(856.76, 43.24) * mm, "end": v(855, 39) * mm});
            skLineSegment(sketch, "E124.9.0.10", {"start": v(857.75, 39) * mm, "end": v(857.75, 16.44) * mm});
            skArc(sketch, "E124.9.0.11", {"start": v(942.25, 39) * mm, "mid": v(941.3, 41.3) * mm, "end": v(939, 42.25) * mm});
            skLineSegment(sketch, "E124.9.0.12", {"start": v(939, 45) * mm, "end": v(861, 45) * mm});
            skLineSegment(sketch, "E124.9.0.13", {"start": v(942.25, 16.44) * mm, "end": v(942.25, 39) * mm});
            skLineSegment(sketch, "E124.9.0.14", {"start": v(910.99, 42.25) * mm, "end": v(889.01, 42.25) * mm});
            skArc(sketch, "E124.9.0.15", {"start": v(885.5, 39.73) * mm, "mid": v(885.15, 41.47) * mm, "end": v(883.56, 42.25) * mm});
            skLineSegment(sketch, "E124.9.0.16", {"start": v(939, 42.25) * mm, "end": v(916.44, 42.25) * mm});
            skLineSegment(sketch, "E124.9.0.17", {"start": v(924.26, 15.8) * mm, "end": v(943.43, 10.67) * mm});
            skArc(sketch, "E124.9.0.18", {"start": v(939.73, 14.5) * mm, "mid": v(941.47, 14.85) * mm, "end": v(942.25, 16.44) * mm});
            skLineSegment(sketch, "E124.9.0.19", {"start": v(883.56, 42.25) * mm, "end": v(861, 42.25) * mm});
            skArc(sketch, "E124.9.0.20", {"start": v(891.14, -23.09) * mm, "mid": v(900, -25) * mm, "end": v(908.86, -23.09) * mm});
            skLineSegment(sketch, "E124.9.0.21", {"start": v(860.27, 14.5) * mm, "end": v(875.52, 18.6) * mm});
            skArc(sketch, "E124.9.0.22", {"start": v(857.75, 16.44) * mm, "mid": v(858.53, 14.85) * mm, "end": v(860.27, 14.5) * mm});
            skArc(sketch, "E124.9.0.23", {"start": v(908.86, 23.09) * mm, "mid": v(909.06, 23.02) * mm, "end": v(909.27, 23) * mm});
            skArc(sketch, "E124.9.0.24", {"start": v(920.25, 7.4) * mm, "mid": v(920.26, 7.23) * mm, "end": v(920.3, 7.07) * mm});
            skArc(sketch, "E124.9.0.25", {"start": v(914.5, -39.73) * mm, "mid": v(914.85, -41.47) * mm, "end": v(916.44, -42.25) * mm});
            skArc(sketch, "E124.9.0.26", {"start": v(920.53, -23) * mm, "mid": v(919.3, -23.41) * mm, "end": v(918.6, -24.48) * mm});
            skArc(sketch, "E124.9.0.27", {"start": v(879.75, -7.4) * mm, "mid": v(879.74, -7.23) * mm, "end": v(879.7, -7.07) * mm});
            skArc(sketch, "E124.9.0.28", {"start": v(939, -42.25) * mm, "mid": v(941.3, -41.3) * mm, "end": v(942.25, -39) * mm});
            skLineSegment(sketch, "E124.9.0.29", {"start": v(916.44, -42.25) * mm, "end": v(939, -42.25) * mm});
            skArc(sketch, "E124.9.0.30", {"start": v(945, -11.88) * mm, "mid": v(944.51, -10.89) * mm, "end": v(943.43, -10.67) * mm});
            skArc(sketch, "E124.9.0.31", {"start": v(883.56, -42.25) * mm, "mid": v(885.15, -41.47) * mm, "end": v(885.5, -39.73) * mm});
            skArc(sketch, "E124.9.0.32", {"start": v(855, 11.88) * mm, "mid": v(855.49, 10.89) * mm, "end": v(856.57, 10.67) * mm});
            skLineSegment(sketch, "E124.9.0.33", {"start": v(880.75, -20.25) * mm, "end": v(892.6, -20.25) * mm});
            skArc(sketch, "E124.9.0.34", {"start": v(908.86, 23.09) * mm, "mid": v(900, 25) * mm, "end": v(891.14, 23.09) * mm});
            skArc(sketch, "E124.9.0.35", {"start": v(939, -45) * mm, "mid": v(943.24, -43.24) * mm, "end": v(945, -39) * mm});
            skLineSegment(sketch, "E124.9.0.36", {"start": v(939.73, -14.5) * mm, "end": v(924.48, -18.6) * mm});
            skLineSegment(sketch, "E124.9.0.37", {"start": v(924.48, 18.6) * mm, "end": v(939.73, 14.5) * mm});
            skArc(sketch, "E124.9.0.38", {"start": v(920.3, -7.07) * mm, "mid": v(920.26, -7.23) * mm, "end": v(920.25, -7.4) * mm});
            skArc(sketch, "E124.9.0.39", {"start": v(916.44, 42.25) * mm, "mid": v(914.85, 41.47) * mm, "end": v(914.5, 39.73) * mm});
            skArc(sketch, "E124.9.0.40", {"start": v(923.09, -8.86) * mm, "mid": v(925, 0) * mm, "end": v(923.09, 8.86) * mm});
            skArc(sketch, "E124.9.0.41", {"start": v(918.6, 24.48) * mm, "mid": v(919.3, 23.41) * mm, "end": v(920.53, 23) * mm});
            skArc(sketch, "E124.9.0.42", {"start": v(856.57, -10.67) * mm, "mid": v(855.49, -10.89) * mm, "end": v(855, -11.88) * mm});
            skLineSegment(sketch, "E124.9.0.43", {"start": v(877, -21) * mm, "end": v(877, -20.53) * mm});
            skLineSegment(sketch, "E124.9.0.44", {"start": v(861, -42.25) * mm, "end": v(883.56, -42.25) * mm});
            skLineSegment(sketch, "E124.9.0.45", {"start": v(885.16, 23) * mm, "end": v(890.73, 23) * mm});
            skLineSegment(sketch, "E124.9.0.46", {"start": v(892.6, 20.25) * mm, "end": v(880.75, 20.25) * mm});
            skLineSegment(sketch, "E124.9.0.47", {"start": v(945, -39) * mm, "end": v(945, -11.88) * mm});
            skLineSegment(sketch, "E124.9.0.48", {"start": v(889.01, -42.25) * mm, "end": v(910.99, -42.25) * mm});
            skLineSegment(sketch, "E124.9.0.49", {"start": v(889.01, 42.25) * mm, "end": v(884.2, 24.26) * mm});
            skLineSegment(sketch, "E124.9.0.50", {"start": v(877, 14.84) * mm, "end": v(877, 9.27) * mm});
            skArc(sketch, "E124.9.0.51", {"start": v(920.25, 19.25) * mm, "mid": v(919.96, 19.96) * mm, "end": v(919.25, 20.25) * mm});
            skArc(sketch, "E124.9.0.52", {"start": v(892.93, -20.3) * mm, "mid": v(900, -21.5) * mm, "end": v(907.07, -20.3) * mm});
            skArc(sketch, "E124.9.0.53", {"start": v(907.07, 20.3) * mm, "mid": v(900, 21.5) * mm, "end": v(892.93, 20.3) * mm});
            skArc(sketch, "E124.9.0.54", {"start": v(877, -21) * mm, "mid": v(877.59, -22.41) * mm, "end": v(879, -23) * mm});
            skLineSegment(sketch, "E124.9.0.55", {"start": v(881.4, 24.48) * mm, "end": v(885.5, 39.73) * mm});
            skArc(sketch, "E124.9.0.56", {"start": v(907.4, -20.25) * mm, "mid": v(907.23, -20.26) * mm, "end": v(907.07, -20.3) * mm});
            skLineSegment(sketch, "E124.9.0.57", {"start": v(919.25, 20.25) * mm, "end": v(907.4, 20.25) * mm});
            skArc(sketch, "E124.9.0.58", {"start": v(876.91, 8.86) * mm, "mid": v(876.98, 9.06) * mm, "end": v(877, 9.27) * mm});
            skArc(sketch, "E124.9.0.59", {"start": v(919.25, -20.25) * mm, "mid": v(919.96, -19.96) * mm, "end": v(920.25, -19.25) * mm});
            skArc(sketch, "E124.9.0.60", {"start": v(923.09, -8.86) * mm, "mid": v(923.02, -9.06) * mm, "end": v(923, -9.27) * mm});
            skLineSegment(sketch, "E124.9.0.61", {"start": v(914.5, 39.73) * mm, "end": v(918.6, 24.48) * mm});
            skArc(sketch, "E124.9.0.62", {"start": v(880.75, 20.25) * mm, "mid": v(880.04, 19.96) * mm, "end": v(879.75, 19.25) * mm});
            skLineSegment(sketch, "E124.9.0.63", {"start": v(856.57, 10.67) * mm, "end": v(875.74, 15.8) * mm});
            skLineSegment(sketch, "E124.9.0.64", {"start": v(920.25, 7.4) * mm, "end": v(920.25, 19.25) * mm});
            skLineSegment(sketch, "E124.9.0.65", {"start": v(942.25, -39) * mm, "end": v(942.25, -16.44) * mm});
            skArc(sketch, "E124.9.0.66", {"start": v(891.14, -23.09) * mm, "mid": v(890.94, -23.02) * mm, "end": v(890.73, -23) * mm});
            skArc(sketch, "E124.9.0.67", {"start": v(920.3, -7.07) * mm, "mid": v(921.5, 0) * mm, "end": v(920.3, 7.07) * mm});
            skArc(sketch, "E124.9.0.68", {"start": v(860.27, -14.5) * mm, "mid": v(858.53, -14.85) * mm, "end": v(857.75, -16.44) * mm});
            skArc(sketch, "E124.9.0.69", {"start": v(943.43, 10.67) * mm, "mid": v(944.51, 10.89) * mm, "end": v(945, 11.88) * mm});
            skArc(sketch, "E124.9.0.70", {"start": v(890.73, 23) * mm, "mid": v(890.94, 23.02) * mm, "end": v(891.14, 23.09) * mm});
            skLineSegment(sketch, "E124.9.0.71", {"start": v(943.43, -10.67) * mm, "end": v(924.26, -15.8) * mm});
            skLineSegment(sketch, "E124.9.0.72", {"start": v(914.84, -23) * mm, "end": v(909.27, -23) * mm});
            skLineSegment(sketch, "E124.9.0.73", {"start": v(885.5, -39.73) * mm, "end": v(881.4, -24.48) * mm});
            skLineSegment(sketch, "E124.9.0.74", {"start": v(910.99, -42.25) * mm, "end": v(915.8, -24.26) * mm});
            skLineSegment(sketch, "E124.9.0.75", {"start": v(879.75, -7.4) * mm, "end": v(879.75, -19.25) * mm});
            skLineSegment(sketch, "E124.9.0.76", {"start": v(877, -9.27) * mm, "end": v(877, -14.84) * mm});
            skLineSegment(sketch, "E124.9.0.77", {"start": v(921, -23) * mm, "end": v(920.53, -23) * mm});
            skArc(sketch, "E124.9.0.78", {"start": v(915.8, -24.26) * mm, "mid": v(915.64, -23.4) * mm, "end": v(914.84, -23) * mm});
            skArc(sketch, "E124.9.0.79", {"start": v(914.84, 23) * mm, "mid": v(915.64, 23.4) * mm, "end": v(915.8, 24.26) * mm});
            skArc(sketch, "E124.9.0.80", {"start": v(879, 23) * mm, "mid": v(877.59, 22.41) * mm, "end": v(877, 21) * mm});
            skLineSegment(sketch, "E124.9.0.81", {"start": v(918.6, -24.48) * mm, "end": v(914.5, -39.73) * mm});
            skArc(sketch, "E124.9.0.82", {"start": v(876.91, 8.86) * mm, "mid": v(875, 0) * mm, "end": v(876.91, -8.86) * mm});
            skArc(sketch, "E124.9.0.83", {"start": v(923, -14.84) * mm, "mid": v(923.4, -15.64) * mm, "end": v(924.26, -15.8) * mm});
            skArc(sketch, "E124.9.0.84", {"start": v(892.6, 20.25) * mm, "mid": v(892.77, 20.26) * mm, "end": v(892.93, 20.3) * mm});
            skLineSegment(sketch, "E124.9.0.85", {"start": v(879.47, -23) * mm, "end": v(879, -23) * mm});
            skLineSegment(sketch, "E124.9.0.86", {"start": v(915.8, 24.26) * mm, "end": v(910.99, 42.25) * mm});
            skArc(sketch, "E124.9.0.87", {"start": v(923, 20.53) * mm, "mid": v(923.41, 19.3) * mm, "end": v(924.48, 18.6) * mm});
            skArc(sketch, "E124.9.0.88", {"start": v(909.27, -23) * mm, "mid": v(909.06, -23.02) * mm, "end": v(908.86, -23.09) * mm});
            skLineSegment(sketch, "E124.9.0.89", {"start": v(884.2, -24.26) * mm, "end": v(889.01, -42.25) * mm});
            skArc(sketch, "E124.9.0.90", {"start": v(892.93, -20.3) * mm, "mid": v(892.77, -20.26) * mm, "end": v(892.6, -20.25) * mm});
            skArc(sketch, "E124.9.0.91", {"start": v(942.25, -16.44) * mm, "mid": v(941.47, -14.85) * mm, "end": v(939.73, -14.5) * mm});
            skLineSegment(sketch, "E124.9.0.92", {"start": v(875.52, -18.6) * mm, "end": v(860.27, -14.5) * mm});
            skLineSegment(sketch, "E124.9.0.93", {"start": v(923, 9.27) * mm, "end": v(923, 14.84) * mm});
            skArc(sketch, "E124.9.0.94", {"start": v(907.07, 20.3) * mm, "mid": v(907.23, 20.26) * mm, "end": v(907.4, 20.25) * mm});
            skLineSegment(sketch, "E124.9.0.95", {"start": v(909.27, 23) * mm, "end": v(914.84, 23) * mm});
            skArc(sketch, "E124.9.0.96", {"start": v(921, -23) * mm, "mid": v(922.41, -22.41) * mm, "end": v(923, -21) * mm});
            skArc(sketch, "E124.9.0.97", {"start": v(877, -20.53) * mm, "mid": v(876.59, -19.3) * mm, "end": v(875.52, -18.6) * mm});
            skLineSegment(sketch, "E124.9.0.98", {"start": v(879, 23) * mm, "end": v(879.47, 23) * mm});
            skLineSegment(sketch, "E124.9.0.99", {"start": v(920.25, -19.25) * mm, "end": v(920.25, -7.4) * mm});
            skArc(sketch, "E124.9.0.100", {"start": v(884.2, 24.26) * mm, "mid": v(884.36, 23.4) * mm, "end": v(885.16, 23) * mm});
            skLineSegment(sketch, "E124.9.0.101", {"start": v(907.4, -20.25) * mm, "end": v(919.25, -20.25) * mm});
            skLineSegment(sketch, "E124.9.0.102", {"start": v(923, 21) * mm, "end": v(923, 20.53) * mm});
            skLineSegment(sketch, "E124.9.0.103", {"start": v(890.73, -23) * mm, "end": v(885.16, -23) * mm});
            skLineSegment(sketch, "E124.9.0.104", {"start": v(875.74, -15.8) * mm, "end": v(856.57, -10.67) * mm});
            skArc(sketch, "E124.9.0.105", {"start": v(879.7, 7.07) * mm, "mid": v(878.5, 0) * mm, "end": v(879.7, -7.07) * mm});
            skArc(sketch, "E124.9.0.106", {"start": v(923, 9.27) * mm, "mid": v(923.02, 9.06) * mm, "end": v(923.09, 8.86) * mm});
            skArc(sketch, "E124.9.0.107", {"start": v(881.4, -24.48) * mm, "mid": v(880.7, -23.41) * mm, "end": v(879.47, -23) * mm});
            skLineSegment(sketch, "E124.9.0.108", {"start": v(923, -20.53) * mm, "end": v(923, -21) * mm});
            skArc(sketch, "E124.9.0.109", {"start": v(879.47, 23) * mm, "mid": v(880.7, 23.41) * mm, "end": v(881.4, 24.48) * mm});
            skArc(sketch, "E124.9.0.110", {"start": v(877, -9.27) * mm, "mid": v(876.98, -9.06) * mm, "end": v(876.91, -8.86) * mm});
            skLineSegment(sketch, "E124.9.0.111", {"start": v(923, -14.84) * mm, "end": v(923, -9.27) * mm});
            skLineSegment(sketch, "E124.9.0.112", {"start": v(920.53, 23) * mm, "end": v(921, 23) * mm});
            skArc(sketch, "E124.9.0.113", {"start": v(875.52, 18.6) * mm, "mid": v(876.59, 19.3) * mm, "end": v(877, 20.53) * mm});
            skArc(sketch, "E124.9.0.114", {"start": v(885.16, -23) * mm, "mid": v(884.36, -23.4) * mm, "end": v(884.2, -24.26) * mm});
            skArc(sketch, "E124.9.0.115", {"start": v(875.74, -15.8) * mm, "mid": v(876.6, -15.64) * mm, "end": v(877, -14.84) * mm});
            skArc(sketch, "E124.9.0.116", {"start": v(924.48, -18.6) * mm, "mid": v(923.41, -19.3) * mm, "end": v(923, -20.53) * mm});
            skLineSegment(sketch, "E124.9.0.117", {"start": v(879.75, 19.25) * mm, "end": v(879.75, 7.4) * mm});
            skArc(sketch, "E124.9.0.118", {"start": v(879.75, -19.25) * mm, "mid": v(880.04, -19.96) * mm, "end": v(880.75, -20.25) * mm});
            skArc(sketch, "E124.9.0.119", {"start": v(923, 21) * mm, "mid": v(922.41, 22.41) * mm, "end": v(921, 23) * mm});
            skArc(sketch, "E124.9.0.120", {"start": v(924.26, 15.8) * mm, "mid": v(923.4, 15.64) * mm, "end": v(923, 14.84) * mm});
            skArc(sketch, "E124.9.0.121", {"start": v(877, 14.84) * mm, "mid": v(876.6, 15.64) * mm, "end": v(875.74, 15.8) * mm});
            skArc(sketch, "E124.9.0.122", {"start": v(879.7, 7.07) * mm, "mid": v(879.74, 7.23) * mm, "end": v(879.75, 7.4) * mm});
            skLineSegment(sketch, "E124.9.0.123", {"start": v(877, 20.53) * mm, "end": v(877, 21) * mm});
            skLineSegment(sketch, "E124.direction1", {"start": v(-39, -45) * mm, "end": v(61, -45) * mm, "construction": true});
            skSolve(sketch);
        }
        {
            var Q0;
            Q0=makeQuery(id+"F0.imprint","IMPRINT",FACE,{"disambiguationData":[TD([[makeQuery(id+"F0.imprint","IMPRINT",EDGE,{"derivedFrom":sQuery(id+"F0.wireOp",EDGE,"E0")}),-1.0]])]});
            extrude(context, id + "F1", {"entities" : qUnion([Q0]), "depth" : 1000 * mm, "offsetDistance" : 25 * mm});
        }
    });
